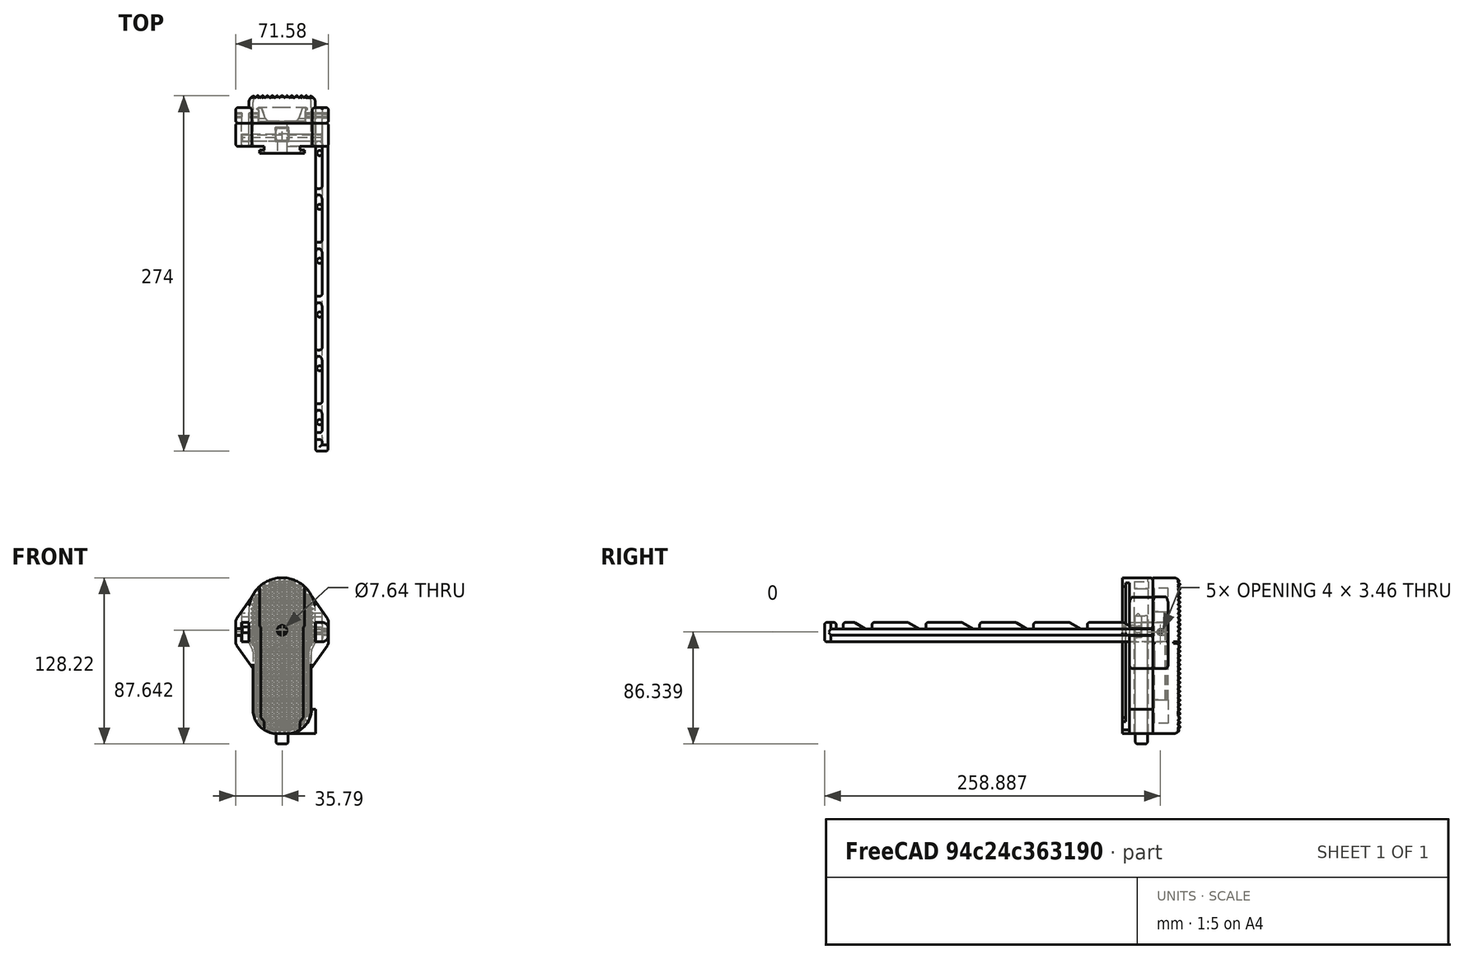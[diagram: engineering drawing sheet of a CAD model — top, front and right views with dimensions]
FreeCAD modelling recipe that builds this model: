
FCSTD DOCUMENT  (FreeCAD 0.19R24291 (Git))
Label: TelescopingButtExtensionPlasticArmsV2
License: All rights reserved
LicenseURL: http://en.wikipedia.org/wiki/All_rights_reserved
objects: Sketcher::SketchObject×34, PartDesign::Pocket×17, PartDesign::Pad×14, PartDesign::Fillet×10, PartDesign::Body×8, Spreadsheet::Sheet×5, PartDesign::Mirrored×4, PartDesign::LinearPattern×3, App::Part×3, Part::Mirroring×2, PartDesign::SubtractivePipe×1, PartDesign::AdditivePipe×1, PartDesign::Groove×1, PartDesign::Chamfer×1
note: 141 computed .brp shape members not serialized (recipe doc carries the construction recipe); baked Part::Feature solids carry a one-line shape summary decoded from their .brp

FEATURE [Spreadsheet::Sheet] Spreadsheet  label="P90Measurements"
  cells = A1=ButtDovetail; D1=Overall; G1=ButtPad; I1=Reference Point; J1=Bottom of pad, just at base of dovetail body; L1=SpaceForTelescopingBar; M1(SpaceForTelescopingBar)==0.584"; A2=DovetailHeight; B2(DovetailHeight)==5mm; D2=ButtOverallHeight; E2(ButtOverallHeight)==4.733"; G2=PadWidestWidth; H2(PadWidestWidth)==2.017"; A3=DovetailBodyWidth; B3(DovetailBodyWidth)==28mm; D3=PadBCGHoleFromReferencePoint; E3(PadBCGHoleFromReferencePoint)==2.997"; G3=PadThinnestWidth; H3(PadThinnestWidth)==1.772"; A4=DovetailLedgeHeight; B4(DovetailLedgeHeight)==2.5mm; D4=PadBCGHoleDiameter; E4(PadBCGHoleDiameter)==0.277"; G4=PadWidestWidthInnerShoulderDistanceFromReferencePoint; H4(PadWidestWidthInnerShoulderDistanceFromReferencePoint)==2.532"; A5=DovetailLedgeWidestWidth; B5(DovetailLedgeWidestWidth)==35.5mm; D5=PadBCGHoleDepth; E5(PadBCGHoleDepth)==0.375"; G5=PadWidestWidthOuterShoulderDistanceFromReferencePoint; H5(PadWidestWidthOuterShoulderDistanceFromReferencePoint)==2.785"; A6=DovetailLedgeMiddleWidth; B6(DovetailLedgeMiddleWidth)==1.32"; G6=PadBottomWidth; H6(PadBottomWidth)==0.3"; A7=DovetailMiddleWidthInsideShoulderDistanceFromReferencePoint; B7(DovetailMiddleWidthInsideShoulderDistanceFromReferencePoint)==0.37"; A8=DovetailMiddleWidthOutsideShoulderDistanceFromReferencePoint; B8(DovetailMiddleWidthOutsideShoulderDistanceFromReferencePoint)==0.484"; A9=DovetailBottobBodyBevelDistanceFromReferencePoint; B9(DovetailBottobBodyBevelDistanceFromReferencePoint)==0.154"; A10=DovetailWidestLedgeStartingPointFromReferencePoint; B10(DovetailWidestLedgeStartingPointFromReferencePoint)==3.222"
FEATURE [Spreadsheet::Sheet] Spreadsheet001  label="ProjectSettings"
  cells = A1=Tolerance; A2=LooseTolerance; B2(LooseTolerance)==0.3mm; C2=SpringMaxHeight; D2(SpringMaxHeight)==20mm; E2=CrosspinWidth; F2(CrosspinWidth)==4mm; G2=EndcapScrewBodyDiameter; H2(EndcapScrewBodyDiameter)==4mm; I2=LengthFromButtToChargingHandleShelf; J2(LengthFromButtToChargingHandleShelf)==310mm; K2=AdditionalPrinterTolerance; L2(AdditionalPrinterTolerance)==0mm; A3=TightTolerance; B3(TightTolerance)==0.1mm + AdditionalPrinterTolerance; C3=TelescopingPadOAL; D3(TelescopingPadOAL)==TelescopingBarInsertDepth + TelescopingButtThickness; E3=CrosspinHeight; F3(CrosspinHeight)==BarHeight / 3; G3=EndcapScrewHeadDiameter; H3(EndcapScrewHeadDiameter)==6mm; K3=SupportGap; L3(SupportGap)==0.16mm; A4=WallThickness; B4(WallThickness)==4mm; C4=StandardFillet; D4(StandardFillet)==2mm; E4=CrosspinLength; G4=EndcapNutHeight; H4(EndcapNutHeight)==0.273"; A5=LockingButtonWidth; B5(LockingButtonWidth)==10mm; C5=LockingPinWidth; D5(LockingPinWidth)==0.1875"; E5=ButtonActuationDistance; F5(ButtonActuationDistance)==CrosspinHeight * 2; G5=EndcapNutThickness; H5(EndcapNutThickness)==0.121"; A6=LockingButtonHeight; B6(LockingButtonHeight)==10mm; C6=LockingPinHeight; D6(LockingPinHeight)==BarHeight / 3 - LooseTolerance * 2; G6=EndcapSectionOnBarLength; H6(EndcapSectionOnBarLength)==15mm; A7=LockingButtonLength; B7(LockingButtonLength)==60mm; C7=LockingPinLength; D7(LockingPinLength)==40mm; G7=EndcapSectionHangingOffOfBarLength; H7(EndcapSectionHangingOffOfBarLength)==WallThickness; A8=LockingButtonHoleDepth; B8(LockingButtonHoleDepth)==<<P90Measurements>>.PadWidestWidthOuterShoulderDistanceFromReferencePoint + BarThickness + LockingPinHeight * 3 + SpringMaxHeight; C8=BarThickness; D8(BarThickness)==5mm; G8=ScrewCountersinkDepth; H8(ScrewCountersinkDepth)==0.089"; A9=LockingButtonActuationDistance; B9(LockingButtonActuationDistance)==6mm; C9=BarHeight; D9(BarHeight)==15mm; G9=EndcapScrewThreadHeight; H9(EndcapScrewThreadHeight)==8mm; A10=LockingBodyLength; B10(LockingBodyLength)==WallThickness * 2 + LockingButtonHeight; C10=BarLength; D10(BarLength)==265mm; A11=TelescopingPadComfortFilletRadius; B11(TelescopingPadComfortFilletRadius)==5mm; C11=BarNumberOfKnotches; D11(BarNumberOfKnotches)=6; C12=TelescopingBarInsertDepth; D12(TelescopingBarInsertDepth)==WallThickness * 2 + CrosspinWidth; A13=ScallopRadius; B13(ScallopRadius)==1.5mm; C13=TelescopingButtThickness; D13(TelescopingButtThickness)==10mm; A14=DistanceBetweenScallops; B14(DistanceBetweenScallops)==0.25mm; C14=BarDistanceBetweenKnotches; D14(BarDistanceBetweenKnotches)=; C15=BarLastKnotchLocationFromOrigin; D15(BarLastKnotchLocationFromOrigin)==BarLength - EndcapSectionOnBarLength - WallThickness; A16=PaperworkLidNubWidth; B16(PaperworkLidNubWidth)==2mm; C16=BarOccupiedLength; D16(BarOccupiedLength)==WallThickness * 4 + LockingButtonHeight + CrosspinWidth; A17=PaperworkLidNubHeight; B17(PaperworkLidNubHeight)==1.5mm; C17=BarUnoccupiedLength; D17(BarUnoccupiedLength)==BarLength - BarOccupiedLength; A18=PaperworkLidWallThickness; B18(PaperworkLidWallThickness)==2mm; C18=BarRackAngle; D18(BarRackAngle)=150; A19=PaperworkLidFingerHoleDiameter; B19(PaperworkLidFingerHoleDiameter)==20mm; C19=BarRackFillet; D19(BarRackFillet)==2mm; A20=PaperworkLipTabWallFilletRadius; B20(PaperworkLipTabWallFilletRadius)==4mm; C20=BarFillet; D20(BarFillet)==2mm; A21=PaperwokLipInteriorWallAngle; B21(PaperwokLipInteriorWallAngle)=110; C21=BarRackStartOffset; D21(BarRackStartOffset)==TelescopingBarInsertDepth + WallThickness + LockingButtonWidth / 2; A22=PaperworklidbaseThickness; B22(PaperworklidbaseThickness)==1.5mm; C22=BarRackEndoffset; D22(BarRackEndoffset)==WallThickness * 2 + LockingPinWidth + BarThickness; C23=BarRackL:ength; D23(BarRackLength)==13.6mm; A24=LockingButtonHoleClearanceForChamfer; B24(LockingButtonHoleClearanceForChamfer)==min(LockingButtonWidth; LockingButtonHeight) * 9 / 20; C24=BarEndcapThickness; D24(BarEndcapThickness)==BarThickness; A25=LockingPinPocketOverhangCompensationDistance; B25(LockingPinPocketOverhangCompensationDistance)==1.5mm; C25=PadCrosspinLength; D25(PadCrosspinLength)==17mm; A27=LockingBodyPadThickness; B27(LockingBodyPadThickness)==WallThickness * 2 + LockingButtonHeight
FEATURE [Sketcher::SketchObject] Sketch  label="DovetailBodySketch"
  FullyConstrained = true
  MapMode = 5
  Placement = pos=(0,0,0) rot=(1,0,0;1.5708rad)
  Support = -> [XZ_Plane]
  expr: Constraints[10] = <<P90Measurements>>.DovetailBodyWidth - <<ProjectSettings>>.LooseTolerance * 2
  expr: Constraints[9] = <<P90Measurements>>.ButtOverallHeight
  sketch-geometry (4):
    g0: LineSegment StartX=-13.7 StartY=120.218 StartZ=0 EndX=13.7 EndY=120.218 EndZ=0
    g1: LineSegment StartX=13.7 StartY=120.218 StartZ=0 EndX=13.7 EndY=0 EndZ=0
    g2: LineSegment StartX=13.7 StartY=0 StartZ=0 EndX=-13.7 EndY=0 EndZ=0
    g3: LineSegment StartX=-13.7 StartY=0 StartZ=0 EndX=-13.7 EndY=120.218 EndZ=0
  constraints (11):
    c: Coincident(g0,g1)
    c: Coincident(g1,g2)
    c: Coincident(g2,g3)
    c: Coincident(g3,g0)
    c: Horizontal(g0)
    c: Vertical(g1)
    c: Vertical(g3)
    c: PointOnObject(g1,g-1)
    c: Symmetric(g1,g2,g-2)
    c: DistanceY(g1,g1) = 120.218
    c: DistanceX(g0,g0) = 27.4
FEATURE [PartDesign::Pad] Pad  label="DovetailBodyPad"
  Direction = (1,1,1)
  Length = 5.2
  Length2 = 100
  Placement = pos=(0,0,0) rot=(1,0,0;1.5708rad)
  Profile = -> Sketch
  Type = 0
  expr: Length = <<P90Measurements>>.DovetailHeight + <<ProjectSettings>>.TightTolerance * 2
FEATURE [Sketcher::SketchObject] Sketch001  label="DovetailLedgeSketch"
  AttachmentOffset = pos=(0,0,5.2) rot=(0,0,1;0rad)
  FullyConstrained = true
  MapMode = 5
  Placement = pos=(0,-5.2,-1.2e-15) rot=(1,0,0;1.5708rad)
  Support = -> [XZ_Plane]
  expr: .AttachmentOffset.Base.z = <<DovetailBodyPad>>.Length
  expr: Constraints[10] = <<P90Measurements>>.DovetailLedgeWidestWidth - <<ProjectSettings>>.LooseTolerance * 2
  expr: Constraints[9] = <<P90Measurements>>.ButtOverallHeight
  sketch-geometry (4):
    g0: LineSegment StartX=-17.45 StartY=120.218 StartZ=0 EndX=17.45 EndY=120.218 EndZ=0
    g1: LineSegment StartX=17.45 StartY=120.218 StartZ=0 EndX=17.45 EndY=0 EndZ=0
    g2: LineSegment StartX=17.45 StartY=0 StartZ=0 EndX=-17.45 EndY=0 EndZ=0
    g3: LineSegment StartX=-17.45 StartY=0 StartZ=0 EndX=-17.45 EndY=120.218 EndZ=0
  constraints (11):
    c: Coincident(g0,g1)
    c: Coincident(g1,g2)
    c: Coincident(g2,g3)
    c: Coincident(g3,g0)
    c: Horizontal(g0)
    c: Vertical(g1)
    c: Vertical(g3)
    c: PointOnObject(g1,g-1)
    c: Symmetric(g2,g1,g-2)
    c: DistanceY(g1,g1) = 120.218
    c: DistanceX(g0,g0) = 34.9
FEATURE [PartDesign::Pad] Pad001  label="DovetailLedgePad"
  BaseFeature = -> Pad
  Direction = (1,1,1)
  Length = 2.3
  Length2 = 100
  Placement = pos=(0,0,0) rot=(1,0,0;1.5708rad)
  Profile = -> Sketch001
  Refine = true
  Reversed = true
  Type = 0
  expr: Length = <<P90Measurements>>.DovetailLedgeHeight - <<ProjectSettings>>.TightTolerance * 2
FEATURE [Sketcher::SketchObject] Sketch002  label="DovetailLedgeCutSketch"
  FullyConstrained = true
  MapMode = 5
  Placement = pos=(0,0,0) rot=(1,0,0;1.5708rad)
  Support = -> [XZ_Plane]
  expr: Constraints[35] = <<P90Measurements>>.DovetailMiddleWidthOutsideShoulderDistanceFromReferencePoint
  expr: Constraints[33] = <<P90Measurements>>.DovetailLedgeMiddleWidth - <<ProjectSettings>>.LooseTolerance * 2
  expr: Constraints[36] = <<P90Measurements>>.DovetailWidestLedgeStartingPointFromReferencePoint
  expr: Constraints[34] = <<P90Measurements>>.DovetailMiddleWidthInsideShoulderDistanceFromReferencePoint
  expr: Constraints[32] = <<P90Measurements>>.DovetailBodyWidth - <<ProjectSettings>>.LooseTolerance * 2
  expr: Constraints[29] = <<P90Measurements>>.DovetailLedgeWidestWidth - <<ProjectSettings>>.LooseTolerance * 2
  expr: Constraints[28] = <<P90Measurements>>.ButtOverallHeight
  sketch-geometry (16):
    g0: LineSegment StartX=-27.45 StartY=130.218 StartZ=0 EndX=27.45 EndY=130.218 EndZ=0
    g1: LineSegment StartX=27.45 StartY=130.218 StartZ=0 EndX=27.45 EndY=-10 EndZ=0
    g2: LineSegment StartX=27.45 StartY=-10 StartZ=0 EndX=-27.45 EndY=-10 EndZ=0
    g3: LineSegment StartX=-27.45 StartY=-10 StartZ=0 EndX=-27.45 EndY=130.218 EndZ=0
    g4: LineSegment StartX=-13.7 StartY=0 StartZ=0 EndX=13.7 EndY=0 EndZ=0
    g5: LineSegment StartX=13.7 StartY=0 StartZ=0 EndX=13.7 EndY=9.398 EndZ=0
    g6: LineSegment StartX=13.7 StartY=9.398 StartZ=0 EndX=16.464 EndY=12.2936 EndZ=0
    g7: LineSegment StartX=16.464 StartY=12.2936 StartZ=0 EndX=16.464 EndY=81.8388 EndZ=0
    g8: LineSegment StartX=16.464 StartY=81.8388 StartZ=0 EndX=17.45 EndY=82.8598 EndZ=0
    g9: LineSegment StartX=17.45 StartY=82.8598 StartZ=0 EndX=17.45 EndY=120.218 EndZ=0
    g10: LineSegment StartX=17.45 StartY=120.218 StartZ=0 EndX=-17.45 EndY=120.218 EndZ=0
    g11: LineSegment StartX=-17.45 StartY=120.218 StartZ=0 EndX=-17.45 EndY=82.8598 EndZ=0
    g12: LineSegment StartX=-17.45 StartY=82.8598 StartZ=0 EndX=-16.464 EndY=81.8388 EndZ=0
    g13: LineSegment StartX=-16.464 StartY=81.8388 StartZ=0 EndX=-16.464 EndY=12.2936 EndZ=0
    g14: LineSegment StartX=-16.464 StartY=12.2936 StartZ=0 EndX=-13.7 EndY=9.398 EndZ=0
    g15: LineSegment StartX=-13.7 StartY=9.398 StartZ=0 EndX=-13.7 EndY=0 EndZ=0
  constraints (44):
    c: Coincident(g0,g1)
    c: Coincident(g1,g2)
    c: Coincident(g2,g3)
    c: Coincident(g3,g0)
    c: Horizontal(g0)
    c: Horizontal(g2)
    c: Vertical(g1)
    c: Vertical(g3)
    c: PointOnObject(g4,g-1)
    c: Coincident(g4,g5)
    c: Vertical(g5)
    c: Coincident(g5,g6)
    c: Coincident(g6,g7)
    c: Vertical(g7)
    c: Coincident(g7,g8)
    c: Coincident(g8,g9)
    c: Vertical(g9)
    c: Coincident(g9,g10)
    c: Coincident(g10,g11)
    c: Coincident(g11,g12)
    c: Coincident(g12,g13)
    c: Vertical(g13)
    c: Coincident(g13,g14)
    c: Coincident(g14,g15)
    c: Coincident(g15,g4)
    c: Vertical(g15)
    c: Horizontal(g14,g5)
    c: Horizontal(g13,g6)
    c: DistanceY(g4,g9) = 120.218
    c: DistanceX(g10,g10) = 34.9
    c: Symmetric(g10,g9,g-2)
    c: Symmetric(g12,g7,g-2)
    c: DistanceX(g4,g4) = 27.4
    c: DistanceX(g12,g7) = 32.928
    c: DistanceY(g14) = 9.398
    c: DistanceY(g4,g13) = 12.2936
    c: DistanceY(g-1,g7) = 81.8388
    c: DistanceY(g10,g0) = 10
    c: DistanceX(g0,g10) = 10
    c: DistanceX(g9,g1) = 10
    c: DistanceY(g1,g4) = 10
    c: Symmetric(g4,g4,g-2)
    c: Symmetric(g8,g11,g-2)
    c: Angle(g12,g13) = 2.37365
FEATURE [PartDesign::Pocket] Pocket  label="DovetailLedgeCutPocket"
  BaseFeature = -> Pad001
  Length = 5
  Length2 = 100
  Placement = pos=(0,0,0) rot=(1,0,0;1.5708rad)
  Profile = -> Sketch002
  Reversed = true
  Type = 1
FEATURE [Sketcher::SketchObject] Sketch003  label="PadBodySketch"
  FullyConstrained = true
  MapMode = 5
  Placement = pos=(0,0,0) rot=(1,0,0;1.5708rad)
  Support = -> [XZ_Plane]
  expr: Constraints[27] = <<P90Measurements>>.PadWidestWidthInnerShoulderDistanceFromReferencePoint
  expr: Constraints[22] = <<P90Measurements>>.PadWidestWidthOuterShoulderDistanceFromReferencePoint
  expr: Constraints[19] = <<P90Measurements>>.PadThinnestWidth
  expr: Constraints[21] = <<P90Measurements>>.PadWidestWidth
  expr: Constraints[20] = <<P90Measurements>>.ButtOverallHeight
  sketch-geometry (12):
    g0: LineSegment StartX=-22.5044 StartY=0 StartZ=0 EndX=22.5044 EndY=0 EndZ=0
    g1: LineSegment StartX=22.5044 StartY=0 StartZ=0 EndX=22.5044 EndY=63.2152 EndZ=0
    g2: LineSegment StartX=-22.5044 StartY=63.2152 StartZ=0 EndX=-22.5044 EndY=0 EndZ=0
    g3: LineSegment StartX=-25.6159 StartY=120.218 StartZ=0 EndX=25.6159 EndY=120.218 EndZ=0
    g4: LineSegment StartX=25.6159 StartY=120.218 StartZ=0 EndX=25.6159 EndY=70.739 EndZ=0
    g5: LineSegment StartX=-25.6159 StartY=70.739 StartZ=0 EndX=-25.6159 EndY=120.218 EndZ=0
    g6: LineSegment StartX=-25.3621 StartY=69.6414 StartZ=0 EndX=-22.7582 EndY=64.3128 EndZ=0
    g7: LineSegment StartX=25.3621 StartY=69.6414 StartZ=0 EndX=22.7582 EndY=64.3128 EndZ=0
    g8: ArcOfCircle CenterX=-23.1159 CenterY=70.739 CenterZ=0 NormalX=0 NormalY=0 NormalZ=1 AngleXU=0 Radius=2.5 StartAngle=3.14159 EndAngle=3.59612
    g9: ArcOfCircle CenterX=-25.0044 CenterY=63.2152 CenterZ=0 NormalX=0 NormalY=0 NormalZ=1 AngleXU=0 Radius=2.5 StartAngle=2e-16 EndAngle=0.454529
    g10: ArcOfCircle CenterX=23.1159 CenterY=70.739 CenterZ=0 NormalX=0 NormalY=0 NormalZ=1 AngleXU=0 Radius=2.5 StartAngle=5.82866 EndAngle=6.28319
    g11: ArcOfCircle CenterX=25.0044 CenterY=63.2152 CenterZ=0 NormalX=0 NormalY=0 NormalZ=1 AngleXU=0 Radius=2.5 StartAngle=2.68706 EndAngle=3.14159
  constraints (28):
    c: Coincident(g0,g1)
    c: Coincident(g2,g0)
    c: Vertical(g1)
    c: Vertical(g2)
    c: PointOnObject(g0,g-1)
    c: Coincident(g3,g4)
    c: Coincident(g5,g3)
    c: Vertical(g4)
    c: Vertical(g5)
    c: Tangent(g8,g5) = 1.5708
    c: Tangent(g8,g6) = -1.5708
    c: Tangent(g9,g6) = 1.5708
    c: Tangent(g11,g1) = 1.5708
    c: Tangent(g11,g7) = -1.5708
    c: Tangent(g7,g10) = 1.5708
    c: Tangent(g10,g4) = 1.5708
    c: Tangent(g9,g2) = 1.5708
    c: Symmetric(g0,g0,g-2)
    c: Symmetric(g3,g3,g-2)
    c: DistanceX(g0,g0) = 45.0088
    c: DistanceY(g0,g3) = 120.218
    c: DistanceX(g3,g3) = 51.2318
    c: DistanceY(g-1,g8) = 70.739
    c: Symmetric(g7,g6,g-2)
    c: Symmetric(g6,g7,g-2)
    c: Equal(g11,g10)
    c: Diameter(g11) = 5
    c: DistanceY(g6) = 64.3128
FEATURE [PartDesign::Pad] Pad002  label="PadBodyPad"
  BaseFeature = -> Pocket
  Direction = (1,1,1)
  Length = 18
  Length2 = 100
  Placement = pos=(0,0,0) rot=(1,0,0;1.5708rad)
  Profile = -> Sketch003
  Reversed = true
  Type = 0
  expr: Length = <<ProjectSettings>>.LockingBodyPadThickness
FEATURE [Sketcher::SketchObject] Sketch004  label="PadBevelsCutSketch"
  FullyConstrained = true
  MapMode = 5
  Placement = pos=(0,0,0) rot=(1,0,0;1.5708rad)
  Support = -> [XZ_Plane]
  expr: Constraints[32] = <<P90Measurements>>.PadBottomWidth
  expr: Constraints[29] = <<P90Measurements>>.PadWidestWidth
  expr: Constraints[31] = <<P90Measurements>>.PadWidestWidthInnerShoulderDistanceFromReferencePoint - 5mm
  expr: Constraints[30] = <<P90Measurements>>.PadThinnestWidth
  expr: Constraints[27] = <<P90Measurements>>.ButtOverallHeight
  sketch-geometry (15):
    g0: LineSegment StartX=-35.6159 StartY=130.218 StartZ=0 EndX=35.6159 EndY=130.218 EndZ=0
    g1: LineSegment StartX=35.6159 StartY=130.218 StartZ=0 EndX=35.6159 EndY=-10 EndZ=0
    g2: LineSegment StartX=35.6159 StartY=-10 StartZ=0 EndX=-35.6159 EndY=-10 EndZ=0
    g3: LineSegment StartX=-35.6159 StartY=-10 StartZ=0 EndX=-35.6159 EndY=130.218 EndZ=0
    g4: ArcOfCircle CenterX=-3.81 CenterY=18.6944 CenterZ=0 NormalX=0 NormalY=0 NormalZ=1 AngleXU=0 Radius=18.6944 StartAngle=3.14159 EndAngle=4.71239
    g5: ArcOfCircle CenterX=3.81 CenterY=18.6944 CenterZ=0 NormalX=0 NormalY=0 NormalZ=1 AngleXU=0 Radius=18.6944 StartAngle=4.71239 EndAngle=6.28319
    g6: ArcOfCircle CenterX=2.5e-15 CenterY=94.6023 CenterZ=0 NormalX=0 NormalY=0 NormalZ=1 AngleXU=0 Radius=25.6159 StartAngle=1.5708 EndAngle=3.14159
    g7: ArcOfCircle CenterX=2.5e-15 CenterY=94.6023 CenterZ=0 NormalX=0 NormalY=0 NormalZ=1 AngleXU=0 Radius=25.6159 StartAngle=0 EndAngle=1.5708
    g8: LineSegment StartX=-25.6159 StartY=94.6023 StartZ=0 EndX=-25.6159 EndY=59.3128 EndZ=0
    g9: LineSegment StartX=-25.6159 StartY=59.3128 StartZ=0 EndX=-22.5044 EndY=59.3128 EndZ=0
    g10: LineSegment StartX=-22.5044 StartY=59.3128 StartZ=0 EndX=-22.5044 EndY=18.6944 EndZ=0
    g11: LineSegment StartX=-3.81 StartY=0 StartZ=0 EndX=3.81 EndY=0 EndZ=0
    g12: LineSegment StartX=22.5044 StartY=18.6944 StartZ=0 EndX=22.5044 EndY=59.3128 EndZ=0
    g13: LineSegment StartX=22.5044 StartY=59.3128 StartZ=0 EndX=25.6159 EndY=59.3128 EndZ=0
    g14: LineSegment StartX=25.6159 StartY=59.3128 StartZ=0 EndX=25.6159 EndY=94.6023 EndZ=0
  constraints (39):
    c: Coincident(g0,g1)
    c: Coincident(g1,g2)
    c: Coincident(g2,g3)
    c: Coincident(g3,g0)
    c: Horizontal(g0)
    c: Vertical(g1)
    c: Vertical(g3)
    c: Symmetric(g2,g1,g-2)
    c: PointOnObject(g4,g-1)
    c: PointOnObject(g5,g-1)
    c: Vertical(g8)
    c: Coincident(g9,g8)
    c: Vertical(g10)
    c: Vertical(g12)
    c: Coincident(g13,g12)
    c: Vertical(g14)
    c: Coincident(g13,g14)
    c: Horizontal(g13)
    c: Tangent(g6,g8) = -1.5708
    c: Tangent(g7,g14) = -1.5708
    c: Tangent(g10,g4) = -1.5708
    c: Tangent(g11,g4) = -1.5708
    c: Tangent(g11,g5) = -1.5708
    c: Tangent(g12,g5) = -1.5708
    c: Symmetric(g12,g10,g-2)
    c: Symmetric(g8,g13,g-2)
    c: Coincident(g10,g9)
    c: DistanceY(g-1,g7) = 120.218
    c: Equal(g5,g4)
    c: DistanceX(g6,g7) = 51.2318
    c: DistanceX(g9,g12) = 45.0088
    c: DistanceY(g-1,g12) = 59.3128
    c: DistanceX(g11,g11) = 7.62
    c: PointOnObject(g6,g-2)
    c: Tangent(g6,g7) = -1.5708
    c: Equal(g8,g14)
    c: DistanceY(g2,g-1) = 10
    c: DistanceY(g6,g0) = 10
    c: DistanceX(g7,g1) = 10
FEATURE [PartDesign::Pocket] Pocket001  label="PadBevelsCutPocket"
  BaseFeature = -> Pad002
  Length = 5
  Length2 = 100
  Midplane = true
  Placement = pos=(0,0,0) rot=(1,0,0;1.5708rad)
  Profile = -> Sketch004
  Type = 1
FEATURE [Spreadsheet::Sheet] Spreadsheet002  label="TelescopingBarSettings"
  cells = A1=BarOffsetFromCenter; B1(BarOffsetFromCenter)==<<PadBodyPad>>.Length + <<TelescoptingPadBodyPad>>.Length; A2=LengthFromButtToChargingHandleShelf; B2(LengthFromButtToChargingHandleShelf)==310mm; A3=BarLength; B3(BarLength)==270mm; A4=BarThickness; B4(BarThickness)==0.125"; A5=CrosspinThickness; B5(CrosspinThickness)==0.125"; A6=BarHeight; B6(BarHeight)==12.7mm; A7=LockingPinThickness; B7(LockingPinThickness)==0.125"; A8=BarNumberOfKnotches; B8(BarNumberOfKnotches)=6; A9=ScrewCountersinkDepth; B9(ScrewCountersinkDepth)==0.089"; A10=EndcapHexnutHeight; B10(EndcapHexnutHeight)==0.273"; A11=EndcapHexnutThickness; B11(EndcapHexnutThickness)==0.121"; A12=CrosspinHeight; B12(CrosspinHeight)==6mm; A13=LockingPinHeight; B13(LockingPinHeight)==6mm
FEATURE [Sketcher::SketchObject] Sketch008  label="TelescoptingPadBodySketch"
  FullyConstrained = true
  MapMode = 5
  Placement = pos=(0,0,0) rot=(1,0,0;1.5708rad)
  Support = -> [XZ_Plane002]
  expr: Constraints[20] = <<P90Measurements>>.ButtOverallHeight
  expr: Constraints[21] = <<P90Measurements>>.PadWidestWidth
  expr: Constraints[19] = <<P90Measurements>>.PadThinnestWidth
  expr: Constraints[22] = <<P90Measurements>>.PadWidestWidthOuterShoulderDistanceFromReferencePoint
  expr: Constraints[27] = <<P90Measurements>>.PadWidestWidthInnerShoulderDistanceFromReferencePoint
  sketch-geometry (12):
    g0: LineSegment StartX=-22.5044 StartY=0 StartZ=0 EndX=22.5044 EndY=0 EndZ=0
    g1: LineSegment StartX=22.5044 StartY=0 StartZ=0 EndX=22.5044 EndY=63.2152 EndZ=0
    g2: LineSegment StartX=-22.5044 StartY=63.2152 StartZ=0 EndX=-22.5044 EndY=0 EndZ=0
    g3: LineSegment StartX=-25.6159 StartY=120.218 StartZ=0 EndX=25.6159 EndY=120.218 EndZ=0
    g4: LineSegment StartX=25.6159 StartY=120.218 StartZ=0 EndX=25.6159 EndY=70.739 EndZ=0
    g5: LineSegment StartX=-25.6159 StartY=70.739 StartZ=0 EndX=-25.6159 EndY=120.218 EndZ=0
    g6: LineSegment StartX=-25.3621 StartY=69.6414 StartZ=0 EndX=-22.7582 EndY=64.3128 EndZ=0
    g7: LineSegment StartX=25.3621 StartY=69.6414 StartZ=0 EndX=22.7582 EndY=64.3128 EndZ=0
    g8: ArcOfCircle CenterX=-23.1159 CenterY=70.739 CenterZ=0 NormalX=0 NormalY=0 NormalZ=1 AngleXU=0 Radius=2.5 StartAngle=3.14159 EndAngle=3.59612
    g9: ArcOfCircle CenterX=-25.0044 CenterY=63.2152 CenterZ=0 NormalX=0 NormalY=0 NormalZ=1 AngleXU=0 Radius=2.5 StartAngle=0 EndAngle=0.454529
    g10: ArcOfCircle CenterX=23.1159 CenterY=70.739 CenterZ=0 NormalX=0 NormalY=0 NormalZ=1 AngleXU=0 Radius=2.5 StartAngle=5.82866 EndAngle=6.28319
    g11: ArcOfCircle CenterX=25.0044 CenterY=63.2152 CenterZ=0 NormalX=0 NormalY=0 NormalZ=1 AngleXU=0 Radius=2.5 StartAngle=2.68706 EndAngle=3.14159
  constraints (29):
    c: Coincident(g0,g1)
    c: Coincident(g2,g0)
    c: Vertical(g1)
    c: Vertical(g2)
    c: PointOnObject(g0,g-1)
    c: Coincident(g3,g4)
    c: Coincident(g5,g3)
    c: Vertical(g4)
    c: Vertical(g5)
    c: Tangent(g8,g5) = 1.5708
    c: Tangent(g8,g6) = -1.5708
    c: Tangent(g9,g6) = 1.5708
    c: Tangent(g11,g1) = 1.5708
    c: Tangent(g11,g7) = -1.5708
    c: Tangent(g7,g10) = 1.5708
    c: Tangent(g10,g4) = 1.5708
    c: Tangent(g9,g2) = 1.5708
    c: Symmetric(g0,g0,g-2)
    c: Symmetric(g3,g3,g-2)
    c: DistanceX(g0,g0) = 45.0088
    c: DistanceY(g0,g3) = 120.218
    c: DistanceX(g3,g3) = 51.2318
    c: DistanceY(g-1,g8) = 70.739
    c: Symmetric(g7,g6,g-2)
    c: Symmetric(g6,g7,g-2)
    c: Equal(g11,g10)
    c: Diameter(g11) = 5
    c: DistanceY(g6) = 64.3128
    c: Angle(g1,g7) = 2.68706  'PadAngle'
FEATURE [PartDesign::Pad] Pad006  label="TelescoptingPadBodyPad"
  Direction = (1,1,1)
  Length = 21
  Length2 = 100
  Placement = pos=(0,0,0) rot=(1,0,0;1.5708rad)
  Profile = -> Sketch008
  Reversed = true
  Type = 0
  expr: Length = <<ProjectSettings>>.TelescopingBarInsertDepth + <<ProjectSettings>>.WallThickness + <<ProjectSettings>>.TelescopingPadComfortFilletRadius
FEATURE [Sketcher::SketchObject] Sketch009  label="TelescopingPadBevelsCutSketch"
  FullyConstrained = true
  MapMode = 5
  Placement = pos=(0,0,0) rot=(1,0,0;1.5708rad)
  Support = -> [XZ_Plane002]
  expr: Constraints[27] = <<P90Measurements>>.ButtOverallHeight
  expr: Constraints[30] = <<P90Measurements>>.PadThinnestWidth
  expr: Constraints[31] = <<P90Measurements>>.PadWidestWidthInnerShoulderDistanceFromReferencePoint - 5mm
  expr: Constraints[29] = <<P90Measurements>>.PadWidestWidth
  expr: Constraints[32] = <<P90Measurements>>.PadBottomWidth
  sketch-geometry (15):
    g0: LineSegment StartX=-35.6159 StartY=130.218 StartZ=0 EndX=35.6159 EndY=130.218 EndZ=0
    g1: LineSegment StartX=35.6159 StartY=130.218 StartZ=0 EndX=35.6159 EndY=-10 EndZ=0
    g2: LineSegment StartX=35.6159 StartY=-10 StartZ=0 EndX=-35.6159 EndY=-10 EndZ=0
    g3: LineSegment StartX=-35.6159 StartY=-10 StartZ=0 EndX=-35.6159 EndY=130.218 EndZ=0
    g4: ArcOfCircle CenterX=-3.81 CenterY=18.6944 CenterZ=0 NormalX=0 NormalY=0 NormalZ=1 AngleXU=0 Radius=18.6944 StartAngle=3.14159 EndAngle=4.71239
    g5: ArcOfCircle CenterX=3.81 CenterY=18.6944 CenterZ=0 NormalX=0 NormalY=0 NormalZ=1 AngleXU=0 Radius=18.6944 StartAngle=4.71239 EndAngle=6.28319
    g6: ArcOfCircle CenterX=8e-16 CenterY=94.6023 CenterZ=0 NormalX=0 NormalY=0 NormalZ=1 AngleXU=0 Radius=25.6159 StartAngle=1.5708 EndAngle=3.14159
    g7: ArcOfCircle CenterX=8e-16 CenterY=94.6023 CenterZ=0 NormalX=0 NormalY=0 NormalZ=1 AngleXU=0 Radius=25.6159 StartAngle=0 EndAngle=1.5708
    g8: LineSegment StartX=-25.6159 StartY=94.6023 StartZ=0 EndX=-25.6159 EndY=59.3128 EndZ=0
    g9: LineSegment StartX=-25.6159 StartY=59.3128 StartZ=0 EndX=-22.5044 EndY=59.3128 EndZ=0
    g10: LineSegment StartX=-22.5044 StartY=59.3128 StartZ=0 EndX=-22.5044 EndY=18.6944 EndZ=0
    g11: LineSegment StartX=-3.81 StartY=0 StartZ=0 EndX=3.81 EndY=0 EndZ=0
    g12: LineSegment StartX=22.5044 StartY=18.6944 StartZ=0 EndX=22.5044 EndY=59.3128 EndZ=0
    g13: LineSegment StartX=22.5044 StartY=59.3128 StartZ=0 EndX=25.6159 EndY=59.3128 EndZ=0
    g14: LineSegment StartX=25.6159 StartY=59.3128 StartZ=0 EndX=25.6159 EndY=94.6023 EndZ=0
  constraints (39):
    c: Coincident(g0,g1)
    c: Coincident(g1,g2)
    c: Coincident(g2,g3)
    c: Coincident(g3,g0)
    c: Horizontal(g0)
    c: Vertical(g1)
    c: Vertical(g3)
    c: Symmetric(g2,g1,g-2)
    c: PointOnObject(g4,g-1)
    c: PointOnObject(g5,g-1)
    c: Vertical(g8)
    c: Coincident(g9,g8)
    c: Vertical(g10)
    c: Vertical(g12)
    c: Coincident(g13,g12)
    c: Vertical(g14)
    c: Coincident(g13,g14)
    c: Horizontal(g13)
    c: Tangent(g6,g8) = -1.5708
    c: Tangent(g7,g14) = -1.5708
    c: Tangent(g10,g4) = -1.5708
    c: Tangent(g11,g4) = -1.5708
    c: Tangent(g11,g5) = -1.5708
    c: Tangent(g12,g5) = -1.5708
    c: Symmetric(g12,g10,g-2)
    c: Symmetric(g8,g13,g-2)
    c: Coincident(g10,g9)
    c: DistanceY(g-1,g7) = 120.218
    c: Equal(g5,g4)
    c: DistanceX(g6,g7) = 51.2318
    c: DistanceX(g9,g12) = 45.0088
    c: DistanceY(g-1,g12) = 59.3128
    c: DistanceX(g11,g11) = 7.62
    c: PointOnObject(g6,g-2)
    c: Tangent(g6,g7) = -1.5708
    c: Equal(g8,g14)
    c: DistanceY(g2,g-1) = 10
    c: DistanceY(g6,g0) = 10
    c: DistanceX(g7,g1) = 10
FEATURE [PartDesign::Pocket] Pocket002  label="TelescopingPadBevelsCutPocket"
  BaseFeature = -> Pad006
  Length = 5
  Length2 = 100
  Midplane = true
  Placement = pos=(0,0,0) rot=(1,0,0;1.5708rad)
  Profile = -> Sketch009
  Type = 1
FEATURE [Sketcher::SketchObject] Sketch010  label="TelescopingBarInsertArmSketch"
  FullyConstrained = true
  MapMode = 5
  Placement = pos=(0,0,0) rot=(1,0,0;1.5708rad)
  Support = -> [XZ_Plane002]
  expr: Constraints[11] = <<ProjectSettings>>.BarHeight + <<ProjectSettings>>.TightTolerance * 2
  expr: Constraints[13] = <<P90Measurements>>.PadThinnestWidth / 2
  expr: Constraints[8] = <<P90Measurements>>.PadWidestWidth / 2
  expr: Constraints[10] = <<P90Measurements>>.PadWidestWidthOuterShoulderDistanceFromReferencePoint
  expr: Constraints[9] = <<ProjectSettings>>.BarThickness + <<ProjectSettings>>.LooseTolerance * 2
  expr: Constraints[27] = <<ProjectSettings>>.BarThickness + <<ProjectSettings>>.TightTolerance * 2
  sketch-geometry (13):
    g0: LineSegment StartX=31.2159 StartY=70.739 StartZ=0 EndX=31.2159 EndY=85.939 EndZ=0
    g1: LineSegment StartX=30.8159 StartY=85.939 StartZ=0 EndX=25.6159 EndY=85.939 EndZ=0
    g2: LineSegment StartX=25.6159 StartY=85.939 StartZ=0 EndX=25.6159 EndY=70.739 EndZ=0
    g3: LineSegment StartX=25.6159 StartY=70.739 StartZ=0 EndX=30.8159 EndY=70.739 EndZ=0
    g4: LineSegment StartX=35.7859 StartY=70.739 StartZ=0 EndX=35.7859 EndY=86.039 EndZ=0
    g5: LineSegment StartX=22.5044 StartY=106.448 StartZ=0 EndX=22.5044 EndY=50.3301 EndZ=0
    g6: ArcOfCircle CenterX=31.2159 CenterY=70.739 CenterZ=0 NormalX=0 NormalY=0 NormalZ=1 AngleXU=0 Radius=4.57 StartAngle=5.67232 EndAngle=6.28319
    g7: LineSegment StartX=22.5044 StartY=50.3301 StartZ=0 EndX=34.9594 EndY=68.1178 EndZ=0
    g8: LineSegment StartX=22.5044 StartY=106.448 StartZ=0 EndX=34.9594 EndY=88.6602 EndZ=0
    g9: ArcOfCircle CenterX=31.2159 CenterY=86.039 CenterZ=0 NormalX=0 NormalY=0 NormalZ=1 AngleXU=0 Radius=4.57 StartAngle=4e-16 EndAngle=0.610865
    g10: LineSegment StartX=30.8159 StartY=85.939 StartZ=0 EndX=30.8159 EndY=70.739 EndZ=0
    g11: LineSegment StartX=30.8159 StartY=70.739 StartZ=0 EndX=31.2159 EndY=70.739 EndZ=0
    g12: LineSegment StartX=30.8159 StartY=85.939 StartZ=0 EndX=31.2159 EndY=85.939 EndZ=0
  constraints (36):
    c: Vertical(g0)
    c: Horizontal(g1)
    c: Coincident(g1,g2)
    c: Vertical(g2)
    c: Coincident(g2,g3)
    c: Vertical(g5)
    c: Vertical(g4)
    c: Horizontal(g3)
    c: DistanceX(g-1,g2) = 25.6159
    c: DistanceX(g1,g0) = 5.6
    c: DistanceY(g-1,g2) = 70.739
    c: DistanceY(g0,g0) = 15.2
    c: Coincident(g6,g0)
    c: DistanceX(g-1,g5) = 22.5044
    c: Coincident(g7,g5)
    c: Coincident(g8,g5)
    c: Tangent(g6,g4) = -1.5708
    c: Tangent(g7,g6) = -1.5708
    c: Equal(g7,g8)
    c: Angle(g4,g7) = 2.53073
    c: DistanceX(g-1,g4) = 35.7859  'DistanceFromCenterlineToOutsideOfBarInsertArm'
    c: PointOnObject(g9,g0)
    c: DistanceY(g0,g9) = 0.1
    c: Tangent(g9,g8) = 1.5708
    c: Tangent(g9,g4) = -1.5708
    c: Diameter(g9) = 9.14
    c: Vertical(g10)
    c: DistanceX(g1,g10) = 5.2
    c: Coincident(g1,g10)
    c: Coincident(g3,g10)
    c: Coincident(g11,g3)
    c: Coincident(g11,g6)
    c: Coincident(g12,g1)
    c: Coincident(g12,g0)
    c: Horizontal(g12)
    c: Horizontal(g11)
FEATURE [Spreadsheet::Sheet] Spreadsheet003  label="TelescopingPadSettings"
  cells = A1=TelescopingBarInsertDepth; B1(TelescopingBarInsertDepth)==<<ProjectSettings>>.WallThickness * 2 + <<TelescopingBarSettings>>.CrosspinThickness + <<ProjectSettings>>.TightTolerance * 2; A2=TelescopingButtThickness; B2(TelescopingButtThickness)==10mm; A3=TelescopingPadOAL; B3(TelescopingPadOAL)==TelescopingBarInsertDepth + TelescopingButtThickness
FEATURE [PartDesign::Pad] Pad007  label="TelescopingBarInsertArmPad"
  BaseFeature = -> Pocket002
  Direction = (1,1,1)
  Length = 12
  Length2 = 100
  Placement = pos=(0,0,0) rot=(1,0,0;1.5708rad)
  Profile = -> Sketch010
  Reversed = true
  Type = 0
  expr: Length = <<ProjectSettings>>.TelescopingBarInsertDepth
FEATURE [Sketcher::SketchObject] Sketch011  label="CrosspinHoleSketch"
  FullyConstrained = true
  MapMode = 5
  Placement = pos=(0,0,0) rot=(0.57735,0.57735,0.57735;2.0944rad)
  Support = -> [YZ_Plane002]
  expr: Constraints[2] = <<ProjectSettings>>.CrosspinWidth
  expr: Constraints[0] = <<P90Measurements>>.PadWidestWidthOuterShoulderDistanceFromReferencePoint + <<ProjectSettings>>.BarHeight / 2 + <<ProjectSettings>>.TightTolerance
  expr: Constraints[1] = <<TelescopingPadSettings>>.TelescopingBarInsertDepth / 2 + <<ProjectSettings>>.TightTolerance * 2
  sketch-geometry (8):
    g0: Circle CenterX=5.8875 CenterY=78.339 CenterZ=0 NormalX=0 NormalY=0 NormalZ=1 AngleXU=0 Radius=2
    g1: LineSegment StartX=4.8875 StartY=80.0711 StartZ=0 EndX=3.8875 EndY=78.339 EndZ=0
    g2: LineSegment StartX=3.8875 StartY=78.339 StartZ=0 EndX=4.8875 EndY=76.6069 EndZ=0
    g3: LineSegment StartX=4.8875 StartY=76.6069 StartZ=0 EndX=6.8875 EndY=76.6069 EndZ=0
    g4: LineSegment StartX=6.8875 StartY=76.6069 StartZ=0 EndX=7.8875 EndY=78.339 EndZ=0
    g5: LineSegment StartX=7.8875 StartY=78.339 StartZ=0 EndX=6.8875 EndY=80.0711 EndZ=0
    g6: LineSegment StartX=6.8875 StartY=80.0711 StartZ=0 EndX=4.8875 EndY=80.0711 EndZ=0
    g7: Circle CenterX=5.8875 CenterY=78.339 CenterZ=0 NormalX=0 NormalY=0 NormalZ=1 AngleXU=0 Radius=2
  constraints (19):
    c: DistanceY(g-1,g0) = 78.339
    c: DistanceX(g-1,g0) = 5.8875
    c: Diameter(g0) = 4
    c: Coincident(g1,g2)
    c: Coincident(g2,g3)
    c: Coincident(g3,g4)
    c: Coincident(g4,g5)
    c: Coincident(g5,g6)
    c: Coincident(g6,g1)
    c: Equal(g1, g2-g6) x5
    c: PointOnObject(g1,g7)
    c: PointOnObject(g2,g7)
    c: PointOnObject(g3,g7)
    c: PointOnObject(g4,g7)
    c: PointOnObject(g5,g7)
    c: PointOnObject(g6,g7)
    c: Coincident(g7,g0)
    c: Horizontal(g1,g4)
    c: Equal(g7,g0)
FEATURE [PartDesign::Mirrored] Mirrored  label="TelescopingBarInsertArmMirror"
  BaseFeature = -> Pad007
  MirrorPlane = -> Sketch010 [V_Axis]
  Originals = -> [Pad007]
  Placement = pos=(0,0,0) rot=(1,0,0;1.5708rad)
FEATURE [PartDesign::Pocket] Pocket003  label="CrosspinHolePocket"
  BaseFeature = -> Mirrored
  Length = 5
  Length2 = 100
  Midplane = true
  Placement = pos=(0,0,0) rot=(1,0,0;1.5708rad)
  Profile = -> Sketch011
  Type = 1
FEATURE [PartDesign::Fillet] Fillet  label="ComfortFillet"
  Base = -> Pocket003 [Edge86]
  BaseFeature = -> Pocket003
  Placement = pos=(0,0,0) rot=(1,0,0;1.5708rad)
  Radius = 5
  SupportTransform = false
  expr: Radius = <<ProjectSettings>>.TelescopingPadComfortFilletRadius
FEATURE [Spreadsheet::Sheet] Spreadsheet004  label="CentralPadSettings"
  cells = A1=PadThickness; B1(PadThickness)==<<PadBodyPad>>.Length; A2=LockingButtonHoleDepth; B2(LockingButtonHoleDepth)==<<P90Measurements>>.PadWidestWidthOuterShoulderDistanceFromReferencePoint + <<TelescopingBarSettings>>.BarThickness + <<TelescopingBarSettings>>.LockingPinHeight * 3 + SpringMaxHeight; A3=SpringMaxHeight; B3(SpringMaxHeight)==20mm
FEATURE [Sketcher::SketchObject] Sketch014  label="CentralPadTelescopingBarInsertArmSketch"
  FullyConstrained = true
  MapMode = 5
  Placement = pos=(0,0,0) rot=(1,0,0;1.5708rad)
  Support = -> [XZ_Plane]
  expr: Constraints[11] = <<ProjectSettings>>.BarThickness + <<ProjectSettings>>.LooseTolerance * 2
  expr: Constraints[12] = <<P90Measurements>>.PadWidestWidthOuterShoulderDistanceFromReferencePoint
  expr: Constraints[10] = <<P90Measurements>>.PadWidestWidth / 2
  expr: Constraints[13] = <<ProjectSettings>>.BarHeight + <<ProjectSettings>>.TightTolerance * 2
  expr: Constraints[16] = <<P90Measurements>>.PadThinnestWidth / 2
  expr: Constraints[34] = <<ProjectSettings>>.BarHeight / 3 + <<ProjectSettings>>.TightTolerance * 2
  sketch-geometry (14):
    g0: LineSegment StartX=31.2159 StartY=70.739 StartZ=0 EndX=31.2159 EndY=75.739 EndZ=0
    g1: LineSegment StartX=31.2159 StartY=85.939 StartZ=0 EndX=25.6159 EndY=85.939 EndZ=0
    g2: LineSegment StartX=25.6159 StartY=85.939 StartZ=0 EndX=25.6159 EndY=70.739 EndZ=0
    g3: LineSegment StartX=25.6159 StartY=70.739 StartZ=0 EndX=31.2159 EndY=70.739 EndZ=0
    g4: LineSegment StartX=35.7859 StartY=70.739 StartZ=0 EndX=35.7859 EndY=75.739 EndZ=0
    g5: LineSegment StartX=22.5044 StartY=106.348 StartZ=0 EndX=22.5044 EndY=50.3301 EndZ=0
    g6: ArcOfCircle CenterX=31.2159 CenterY=85.939 CenterZ=0 NormalX=0 NormalY=0 NormalZ=1 AngleXU=0 Radius=4.57 StartAngle=2.3e-15 EndAngle=0.610865
    g7: ArcOfCircle CenterX=31.2159 CenterY=70.739 CenterZ=0 NormalX=0 NormalY=0 NormalZ=1 AngleXU=0 Radius=4.57 StartAngle=5.67232 EndAngle=6.28319
    g8: LineSegment StartX=22.5044 StartY=50.3301 StartZ=0 EndX=34.9594 EndY=68.1178 EndZ=0
    g9: LineSegment StartX=22.5044 StartY=106.348 StartZ=0 EndX=34.9594 EndY=88.5602 EndZ=0
    g10: LineSegment StartX=31.2159 StartY=80.939 StartZ=0 EndX=35.7859 EndY=80.939 EndZ=0
    g11: LineSegment StartX=31.2159 StartY=75.739 StartZ=0 EndX=35.7859 EndY=75.739 EndZ=0
    g12: LineSegment StartX=31.2159 StartY=80.939 StartZ=0 EndX=31.2159 EndY=85.939 EndZ=0
    g13: LineSegment StartX=35.7859 StartY=80.939 StartZ=0 EndX=35.7859 EndY=85.939 EndZ=0
  constraints (38):
    c: Vertical(g0)
    c: Coincident(g12,g1)
    c: Horizontal(g1)
    c: Coincident(g1,g2)
    c: Vertical(g2)
    c: Coincident(g2,g3)
    c: Coincident(g3,g0)
    c: Vertical(g5)
    c: Vertical(g4)
    c: Horizontal(g3)
    c: DistanceX(g-1,g2) = 25.6159
    c: DistanceX(g1,g1) = 5.6
    c: DistanceY(g-1,g2) = 70.739
    c: DistanceY(g0,g12) = 15.2
    c: Coincident(g6,g12)
    c: Coincident(g7,g0)
    c: DistanceX(g-1,g5) = 22.5044
    c: Coincident(g8,g5)
    c: Coincident(g9,g5)
    c: Tangent(g7,g4) = -1.5708
    c: Tangent(g9,g6) = 1.5708
    c: Tangent(g8,g7) = -1.5708
    c: Diameter(g6) = 9.14
    c: Equal(g8,g9)
    c: Angle(g4,g8) = 2.53073
    c: Horizontal(g11)
    c: Horizontal(g10)
    c: Coincident(g0,g11)
    c: Coincident(g12,g10)
    c: Tangent(g0,g12)
    c: Coincident(g4,g11)
    c: Coincident(g13,g10)
    c: Tangent(g4,g13)
    c: Tangent(g6,g13) = -1.5708
    c: DistanceY(g4,g10) = 5.2
    c: Equal(g12,g0)
    c: Angle(g5,g9) = 0.610865  'BarArmAngle'
    c: DistanceX(g10,g10) = 4.57  'BarArmWallThickness'
FEATURE [PartDesign::Pad] Pad008  label="CentralPadTelescopingBarInsertArmPad"
  BaseFeature = -> Pocket001
  Direction = (1,1,1)
  Length = 18
  Length2 = 100
  Placement = pos=(0,0,0) rot=(1,0,0;1.5708rad)
  Profile = -> Sketch014
  Reversed = true
  Type = 0
  expr: Length = <<CentralPadSettings>>.PadThickness
FEATURE [PartDesign::Mirrored] Mirrored001  label="CentralPadTelescopingBarInsertArmMirror"
  BaseFeature = -> Pad008
  MirrorPlane = -> Sketch014 [V_Axis]
  Originals = -> [Pad008]
  Placement = pos=(0,0,0) rot=(1,0,0;1.5708rad)
FEATURE [Sketcher::SketchObject] Sketch017  label="LockingPinBodySketch"
  FullyConstrained = true
  MapMode = 5
  Placement = pos=(0,0,0) rot=(0.57735,0.57735,0.57735;2.0944rad)
  Support = -> [YZ_Plane005]
  expr: Constraints[9] = <<ProjectSettings>>.LockingPinHeight
  expr: Constraints[6] = <<ProjectSettings>>.LockingPinWidth
  sketch-geometry (4):
    g0: LineSegment StartX=-2.38125 StartY=2.2 StartZ=0 EndX=2.38125 EndY=2.2 EndZ=0
    g1: LineSegment StartX=2.38125 StartY=2.2 StartZ=0 EndX=2.38125 EndY=-2.2 EndZ=0
    g2: LineSegment StartX=2.38125 StartY=-2.2 StartZ=0 EndX=-2.38125 EndY=-2.2 EndZ=0
    g3: LineSegment StartX=-2.38125 StartY=-2.2 StartZ=0 EndX=-2.38125 EndY=2.2 EndZ=0
  constraints (10):
    c: Coincident(g0,g1)
    c: Coincident(g1,g2)
    c: Coincident(g2,g3)
    c: Coincident(g3,g0)
    c: Horizontal(g2)
    c: Vertical(g1)
    c: DistanceX(g0,g0) = 4.7625
    c: Symmetric(g2,g0,g-1)
    c: Symmetric(g0,g0,g-2)
    c: DistanceY(g3,g3) = 4.4
FEATURE [PartDesign::Pad] Pad010  label="LockingPinBodyPad"
  Direction = (1,1,1)
  Length = 61.4468
  Length2 = 100
  Midplane = true
  Placement = pos=(0,0,0) rot=(0.57735,0.57735,0.57735;2.0944rad)
  Profile = -> Sketch017
  Type = 0
  expr: Length = Sketch010.Constraints.DistanceFromCenterlineToOutsideOfBarInsertArm * 2 - <<TelescopingBarSettings>>.BarThickness * 3 - <<ProjectSettings>>.LooseTolerance * 2
FEATURE [Sketcher::SketchObject] Sketch018  label="LockingPinHoleSketch"
  FullyConstrained = true
  MapMode = 5
  Placement = pos=(0,0,0) rot=(0.57735,0.57735,0.57735;2.0944rad)
  Support = -> [YZ_Plane]
  expr: Constraints[8] = <<ProjectSettings>>.LockingPinWidth + <<ProjectSettings>>.LooseTolerance * 2
  expr: Constraints[9] = <<P90Measurements>>.PadWidestWidthOuterShoulderDistanceFromReferencePoint + (<<TelescopingBarSettings>>.BarHeight - <<TelescopingBarSettings>>.LockingPinHeight) / 2
  expr: Constraints[10] = <<ProjectSettings>>.WallThickness
  expr: Constraints[11] = <<P90Measurements>>.PadWidestWidthOuterShoulderDistanceFromReferencePoint + <<TelescopingBarSettings>>.BarHeight + <<TelescopingBarSettings>>.LockingPinHeight + <<ProjectSettings>>.LooseTolerance * 2
  sketch-geometry (4):
    g0: LineSegment StartX=4 StartY=90.039 StartZ=0 EndX=9.3625 EndY=90.039 EndZ=0
    g1: LineSegment StartX=9.3625 StartY=90.039 StartZ=0 EndX=9.3625 EndY=74.089 EndZ=0
    g2: LineSegment StartX=9.3625 StartY=74.089 StartZ=0 EndX=4 EndY=74.089 EndZ=0
    g3: LineSegment StartX=4 StartY=74.089 StartZ=0 EndX=4 EndY=90.039 EndZ=0
  constraints (12):
    c: Coincident(g0,g1)
    c: Coincident(g1,g2)
    c: Coincident(g2,g3)
    c: Coincident(g3,g0)
    c: Horizontal(g0)
    c: Horizontal(g2)
    c: Vertical(g1)
    c: Vertical(g3)
    c: DistanceX(g0,g0) = 5.3625
    c: DistanceY(g-1,g2) = 74.089
    c: DistanceX(g-1,g2) = 4
    c: DistanceY(g-1,g0) = 90.039
FEATURE [PartDesign::Pocket] Pocket007  label="LockingPinHolePocket"
  BaseFeature = -> Mirrored001
  Length = 62.0468
  Length2 = 100
  Midplane = true
  Placement = pos=(0,0,0) rot=(1,0,0;1.5708rad)
  Profile = -> Sketch018
  Type = 0
  expr: Length = <<LockingPinBodyPad>>.Length + <<ProjectSettings>>.LooseTolerance * 2
FEATURE [Sketcher::SketchObject] Sketch019  label="LockingButtonHoleSketch"
  FullyConstrained = true
  MapMode = 5
  Support = -> [XY_Plane]
  expr: Constraints[18] = <<ProjectSettings>>.WallThickness
  expr: Constraints[16] = <<ProjectSettings>>.LockingButtonHeight + <<ProjectSettings>>.LooseTolerance * 2
  expr: Constraints[17] = <<ProjectSettings>>.LockingButtonWidth + <<ProjectSettings>>.LooseTolerance * 2
  expr: Constraints[14] = <<ProjectSettings>>.StandardFillet
  sketch-geometry (8):
    g0: LineSegment StartX=-3.3 StartY=14.6 StartZ=0 EndX=3.3 EndY=14.6 EndZ=0
    g1: LineSegment StartX=5.3 StartY=12.6 StartZ=0 EndX=5.3 EndY=6 EndZ=0
    g2: LineSegment StartX=3.3 StartY=4 StartZ=0 EndX=-3.3 EndY=4 EndZ=0
    g3: LineSegment StartX=-5.3 StartY=6 StartZ=0 EndX=-5.3 EndY=12.6 EndZ=0
    g4: ArcOfCircle CenterX=-3.3 CenterY=12.6 CenterZ=0 NormalX=0 NormalY=0 NormalZ=1 AngleXU=0 Radius=2 StartAngle=1.5708 EndAngle=3.14159
    g5: ArcOfCircle CenterX=3.3 CenterY=12.6 CenterZ=0 NormalX=0 NormalY=0 NormalZ=1 AngleXU=0 Radius=2 StartAngle=0 EndAngle=1.5708
    g6: ArcOfCircle CenterX=3.3 CenterY=6 CenterZ=0 NormalX=0 NormalY=0 NormalZ=1 AngleXU=0 Radius=2 StartAngle=4.71239 EndAngle=6.28319
    g7: ArcOfCircle CenterX=-3.3 CenterY=6 CenterZ=0 NormalX=0 NormalY=0 NormalZ=1 AngleXU=0 Radius=2 StartAngle=3.14159 EndAngle=4.71239
  constraints (19):
    c: Horizontal(g2)
    c: Vertical(g1)
    c: Vertical(g3)
    c: Tangent(g3,g4) = 1.5708
    c: Tangent(g0,g4) = 1.5708
    c: Tangent(g0,g5) = 1.5708
    c: Tangent(g1,g5) = 1.5708
    c: Tangent(g2,g6) = 1.5708
    c: Tangent(g1,g6) = 1.5708
    c: Tangent(g2,g7) = 1.5708
    c: Tangent(g3,g7) = 1.5708
    c: Equal(g7,g4)
    c: Equal(g4,g5)
    c: Equal(g5,g6)
    c: Radius(g5) = 2
    c: Symmetric(g0,g0,g-2)
    c: DistanceY(g2,g0) = 10.6
    c: DistanceX(g3,g1) = 10.6
    c: DistanceY(g-1,g2) = 4
FEATURE [PartDesign::Pocket] Pocket008  label="LockingButtonHolePocket"
  BaseFeature = -> Pocket007
  Length = 111.914
  Length2 = 100
  Placement = pos=(0,0,0) rot=(1,0,0;1.5708rad)
  Profile = -> Sketch019
  Reversed = true
  Type = 0
  expr: Length = <<CentralPadSettings>>.LockingButtonHoleDepth
FEATURE [Sketcher::SketchObject] Sketch020  label="ButtonBodySketch"
  AttachmentOffset = pos=(0,0,2) rot=(0,0,1;0rad)
  FullyConstrained = true
  MapMode = 5
  Placement = pos=(0,0,2) rot=(0,0,1;0rad)
  Support = -> [XY_Plane006]
  expr: Constraints[10] = <<ProjectSettings>>.StandardFillet
  expr: Constraints[16] = <<ProjectSettings>>.LockingButtonWidth - <<ProjectSettings>>.LooseTolerance * 2
  expr: Constraints[17] = <<ProjectSettings>>.LockingButtonWidth - <<ProjectSettings>>.LooseTolerance * 2
  sketch-geometry (8):
    g0: LineSegment StartX=-2.7 StartY=4.7 StartZ=0 EndX=2.7 EndY=4.7 EndZ=0
    g1: LineSegment StartX=4.7 StartY=2.7 StartZ=0 EndX=4.7 EndY=-2.7 EndZ=0
    g2: LineSegment StartX=2.7 StartY=-4.7 StartZ=0 EndX=-2.7 EndY=-4.7 EndZ=0
    g3: LineSegment StartX=-4.7 StartY=-2.7 StartZ=0 EndX=-4.7 EndY=2.7 EndZ=0
    g4: ArcOfCircle CenterX=-2.7 CenterY=2.7 CenterZ=0 NormalX=0 NormalY=0 NormalZ=1 AngleXU=0 Radius=2 StartAngle=1.5708 EndAngle=3.14159
    g5: ArcOfCircle CenterX=2.7 CenterY=2.7 CenterZ=0 NormalX=0 NormalY=0 NormalZ=1 AngleXU=0 Radius=2 StartAngle=0 EndAngle=1.5708
    g6: ArcOfCircle CenterX=2.7 CenterY=-2.7 CenterZ=0 NormalX=0 NormalY=0 NormalZ=1 AngleXU=0 Radius=2 StartAngle=4.71239 EndAngle=6.28319
    g7: ArcOfCircle CenterX=-2.7 CenterY=-2.7 CenterZ=0 NormalX=0 NormalY=0 NormalZ=1 AngleXU=0 Radius=2 StartAngle=3.14159 EndAngle=4.71239
  constraints (18):
    c: Horizontal(g0)
    c: Vertical(g1)
    c: Tangent(g3,g4) = 1.5708
    c: Tangent(g0,g4) = 1.5708
    c: Tangent(g1,g5) = 1.5708
    c: Tangent(g0,g5) = 1.5708
    c: Tangent(g1,g6) = 1.5708
    c: Tangent(g2,g6) = 1.5708
    c: Tangent(g2,g7) = 1.5708
    c: Tangent(g3,g7) = 1.5708
    c: Radius(g4) = 2
    c: Equal(g4,g5)
    c: Equal(g4,g6)
    c: Equal(g4,g7)
    c: Symmetric(g2,g2,g-2)
    c: Symmetric(g3,g3,g-1)
    c: DistanceX(g3,g1) = 9.4
    c: DistanceY(g2,g0) = 9.4
FEATURE [PartDesign::Pad] Pad011  label="ButtonBodyPad"
  Direction = (1,1,1)
  Length = 88.939
  Length2 = 10
  Profile = -> Sketch020
  Type = 4
  expr: Length2 = <<ProjectSettings>>.LockingButtonActuationDistance + 4mm
  expr: Length = <<ProjectSettings>>.LockingButtonHoleDepth - <<ProjectSettings>>.SpringMaxHeight
FEATURE [Sketcher::SketchObject] Sketch021  label="ButtonLockingPinHoleSketch"
  FullyConstrained = true
  MapMode = 5
  Placement = pos=(0,0,0) rot=(0.57735,0.57735,0.57735;2.0944rad)
  Support = -> [YZ_Plane006]
  expr: Constraints[11] = <<ProjectSettings>>.LockingPinHeight + <<ProjectSettings>>.TightTolerance * 2
  expr: Constraints[9] = (<<ProjectSettings>>.LockingButtonWidth - <<ProjectSettings>>.LooseTolerance * 2) / 2
  expr: Constraints[7] = <<ProjectSettings>>.LockingPinWidth + <<ProjectSettings>>.TightTolerance * 2
  expr: Constraints[8] = <<P90Measurements>>.PadWidestWidthOuterShoulderDistanceFromReferencePoint + <<ProjectSettings>>.BarHeight / 2
  sketch-geometry (4):
    g0: LineSegment StartX=-4.7 StartY=82.839 StartZ=0 EndX=0.2625 EndY=82.839 EndZ=0
    g1: LineSegment StartX=0.2625 StartY=82.839 StartZ=0 EndX=0.2625 EndY=78.239 EndZ=0
    g2: LineSegment StartX=0.2625 StartY=78.239 StartZ=0 EndX=-4.7 EndY=78.239 EndZ=0
    g3: LineSegment StartX=-4.7 StartY=78.239 StartZ=0 EndX=-4.7 EndY=82.839 EndZ=0
  constraints (12):
    c: Coincident(g0,g1)
    c: Coincident(g1,g2)
    c: Coincident(g2,g3)
    c: Coincident(g3,g0)
    c: Horizontal(g2)
    c: Vertical(g1)
    c: Vertical(g3)
    c: DistanceX(g0,g0) = 4.9625
    c: DistanceY(g-1,g2) = 78.239
    c: DistanceX(g2,g-1) = 4.7
    c: Horizontal(g0)
    c: DistanceY(g3,g3) = 4.6
FEATURE [PartDesign::Pocket] Pocket009  label="ButtonLockingPinHolePocket"
  BaseFeature = -> Pad011
  Length = 5
  Length2 = 100
  Midplane = true
  Profile = -> Sketch021
  Type = 1
FEATURE [Sketcher::SketchObject] Sketch022  label="BCGHoleSketch"
  AttachmentOffset = pos=(0,0,5.2) rot=(0,0,1;0rad)
  FullyConstrained = true
  MapMode = 5
  Placement = pos=(0,-5.2,-1.2e-15) rot=(1,0,0;1.5708rad)
  Support = -> [XZ_Plane]
  expr: Constraints[1] = <<P90Measurements>>.PadBCGHoleFromReferencePoint + <<P90Measurements>>.PadBCGHoleDiameter / 2
  expr: Constraints[2] = <<P90Measurements>>.PadBCGHoleDiameter + <<ProjectSettings>>.LooseTolerance * 2
  expr: .AttachmentOffset.Base.z = <<DovetailBodyPad>>.Length
  sketch-geometry (1):
    g0: Circle CenterX=0 CenterY=79.6417 CenterZ=0 NormalX=0 NormalY=0 NormalZ=1 AngleXU=0 Radius=3.8179
  constraints (3):
    c: PointOnObject(g0,g-2)
    c: DistanceY(g-1,g0) = 79.6417
    c: Diameter(g0) = 7.6358
FEATURE [PartDesign::Pocket] Pocket010  label="BCGHolePocket"
  BaseFeature = -> Pocket008
  Length = 9.2
  Length2 = 100
  Placement = pos=(0,0,0) rot=(1,0,0;1.5708rad)
  Profile = -> Sketch022
  Refine = true
  Type = 0
  expr: Length = <<DovetailBodyPad>>.Length + <<ProjectSettings>>.WallThickness
FEATURE [Sketcher::SketchObject] Sketch024  label="BarCrosspinHoleSketch001"
  FullyConstrained = true
  MapMode = 5
  Placement = pos=(0,0,0) rot=(0.57735,0.57735,0.57735;2.0944rad)
  Support = -> [YZ_Plane007]
  expr: Constraints[2] = <<ProjectSettings>>.WallThickness + <<ProjectSettings>>.CrosspinWidth / 2 + <<ProjectSettings>>.TightTolerance
  expr: Constraints[1] = <<ProjectSettings>>.CrosspinWidth
  sketch-geometry (8):
    g0: Circle CenterX=-6.1 CenterY=0 CenterZ=0 NormalX=0 NormalY=0 NormalZ=1 AngleXU=0 Radius=2
    g1: LineSegment StartX=-4.1 StartY=-2.6457e-12 StartZ=0 EndX=-5.1 EndY=1.73205 EndZ=0
    g2: LineSegment StartX=-5.1 StartY=1.73205 StartZ=0 EndX=-7.1 EndY=1.73205 EndZ=0
    g3: LineSegment StartX=-7.1 StartY=1.73205 StartZ=0 EndX=-8.1 EndY=-2.6457e-12 EndZ=0
    g4: LineSegment StartX=-8.1 StartY=-2.6457e-12 StartZ=0 EndX=-7.1 EndY=-1.73205 EndZ=0
    g5: LineSegment StartX=-7.1 StartY=-1.73205 StartZ=0 EndX=-5.1 EndY=-1.73205 EndZ=0
    g6: LineSegment StartX=-5.1 StartY=-1.73205 StartZ=0 EndX=-4.1 EndY=-2.6457e-12 EndZ=0
    g7: Circle CenterX=-6.1 CenterY=0 CenterZ=0 NormalX=0 NormalY=0 NormalZ=1 AngleXU=0 Radius=2
  constraints (19):
    c: PointOnObject(g0,g-1)
    c: Diameter(g0) = 4
    c: DistanceX(g0,g-1) = 6.1
    c: Coincident(g1,g2)
    c: Coincident(g2,g3)
    c: Coincident(g3,g4)
    c: Coincident(g4,g5)
    c: Coincident(g5,g6)
    c: Coincident(g6,g1)
    c: Equal(g1, g2-g6) x5
    c: PointOnObject(g1,g7)
    c: PointOnObject(g2,g7)
    c: PointOnObject(g3,g7)
    c: PointOnObject(g4,g7)
    c: PointOnObject(g5,g7)
    c: PointOnObject(g6,g7)
    c: Coincident(g7,g0)
    c: PointOnObject(g6,g0)
    c: Horizontal(g1,g3)
FEATURE [Sketcher::SketchObject] Sketch025  label="MainBarSketch001"
  FullyConstrained = true
  MapMode = 5
  Placement = pos=(0,0,0) rot=(1,0,0;1.5708rad)
  Support = -> [XZ_Plane007]
  expr: Constraints[9] = <<ProjectSettings>>.BarHeight
  expr: Constraints[8] = <<ProjectSettings>>.BarThickness
  sketch-geometry (4):
    g0: LineSegment StartX=-2.5 StartY=7.5 StartZ=0 EndX=2.5 EndY=7.5 EndZ=0
    g1: LineSegment StartX=2.5 StartY=7.5 StartZ=0 EndX=2.5 EndY=-7.5 EndZ=0
    g2: LineSegment StartX=2.5 StartY=-7.5 StartZ=0 EndX=-2.5 EndY=-7.5 EndZ=0
    g3: LineSegment StartX=-2.5 StartY=-7.5 StartZ=0 EndX=-2.5 EndY=7.5 EndZ=0
  constraints (10):
    c: Coincident(g0,g1)
    c: Coincident(g1,g2)
    c: Coincident(g2,g3)
    c: Coincident(g3,g0)
    c: Horizontal(g2)
    c: Vertical(g3)
    c: Symmetric(g1,g0,g-1)
    c: Symmetric(g0,g0,g-2)
    c: DistanceX(g0,g0) = 5
    c: DistanceY(g3,g3) = 15
FEATURE [PartDesign::Pad] Pad013  label="MainBarPad001"
  Direction = (1,1,1)
  Length = 265
  Length2 = 100
  Placement = pos=(0,0,0) rot=(1,0,0;1.5708rad)
  Profile = -> Sketch025
  Type = 0
  expr: Length = <<ProjectSettings>>.BarLength
FEATURE [PartDesign::Pocket] Pocket011  label="BarCrosspinHolePocket001"
  BaseFeature = -> Pad013
  Length = 5
  Length2 = 100
  Midplane = true
  Placement = pos=(0,0,0) rot=(1,0,0;1.5708rad)
  Profile = -> Sketch024
  Type = 1
FEATURE [Sketcher::SketchObject] Sketch027  label="BarRackSketch001"
  FullyConstrained = true
  MapMode = 5
  Placement = pos=(0,0,0) rot=(0.57735,0.57735,0.57735;2.0944rad)
  Support = -> [YZ_Plane007]
  expr: Constraints[18] = <<ProjectSettings>>.BarRackLength
  expr: Constraints[14] = <<ProjectSettings>>.BarRackStartOffset
  expr: Constraints[13] = <<ProjectSettings>>.BarRackFillet
  expr: Constraints[8] = <<ProjectSettings>>.BarRackFillet
  expr: Constraints[3] = <<ProjectSettings>>.BarHeight / 2
  expr: Constraints[4] = <<ProjectSettings>>.BarHeight / 3
  expr: Constraints[2] = <<ProjectSettings>>.LockingPinWidth + <<ProjectSettings>>.TightTolerance * 2
  sketch-geometry (7):
    g0: LineSegment StartX=-35.1371 StartY=-7.5 StartZ=0 EndX=-19 EndY=-7.5 EndZ=0
    g1: LineSegment StartX=-21 StartY=-2.5 StartZ=0 EndX=-25.9625 EndY=-2.5 EndZ=0
    g2: ArcOfCircle CenterX=-35.1371 CenterY=-5.5 CenterZ=0 NormalX=0 NormalY=0 NormalZ=1 AngleXU=0 Radius=2 StartAngle=4.71239 EndAngle=5.23713
    g3: LineSegment StartX=-34.1352 StartY=-7.23091 StartZ=0 EndX=-25.9625 EndY=-2.5 EndZ=0
    g4: LineSegment StartX=-21 StartY=-2.5 StartZ=0 EndX=-21 EndY=-5.5 EndZ=0
    g5: ArcOfCircle CenterX=-19 CenterY=-5.5 CenterZ=0 NormalX=0 NormalY=0 NormalZ=1 AngleXU=0 Radius=2 StartAngle=3.14159 EndAngle=4.71239
    g6: LineSegment StartX=-34.1352 StartY=-7.23091 StartZ=0 EndX=-34.6 EndY=-7.5 EndZ=0
  constraints (19):
    c: Horizontal(g0)
    c: Horizontal(g1)
    c: DistanceX(g1,g1) = 4.9625
    c: DistanceY(g0,g-1) = 7.5
    c: DistanceY(g0,g1) = 5
    c: Tangent(g0,g2) = -1.5708
    c: Coincident(g3,g1)
    c: Tangent(g3,g2) = -1.5708
    c: Radius(g2) = 2
    c: Coincident(g4,g1)
    c: Vertical(g4)
    c: Tangent(g5,g4) = -1.5708
    c: Tangent(g0,g5) = -1.5708
    c: Radius(g5) = 2
    c: DistanceX(g1,g-1) = 21
    c: Coincident(g6,g2)
    c: PointOnObject(g6,g0)
    c: Tangent(g6,g2)
    c: DistanceX(g6,g4) = 13.6
FEATURE [PartDesign::Pocket] Pocket013  label="BarRackPocket001"
  BaseFeature = -> Pocket011
  Length = 5
  Length2 = 100
  Midplane = true
  Placement = pos=(0,0,0) rot=(1,0,0;1.5708rad)
  Profile = -> Sketch027
  Type = 1
FEATURE [Sketcher::SketchObject] Sketch028  label="FinalSlotSketch001"
  FullyConstrained = true
  MapMode = 5
  Placement = pos=(0,0,0) rot=(0.57735,0.57735,0.57735;2.0944rad)
  Support = -> [YZ_Plane007]
  expr: Constraints[14] = <<ProjectSettings>>.BarRackFillet
  expr: Constraints[3] = -1 * <<ProjectSettings>>.BarHeight / 2
  expr: Constraints[4] = <<ProjectSettings>>.BarHeight / 3
  expr: Constraints[2] = <<ProjectSettings>>.LockingPinWidth + <<ProjectSettings>>.LooseTolerance * 2
  expr: Constraints[5] = <<ProjectSettings>>.BarLength - <<ProjectSettings>>.BarThickness - <<ProjectSettings>>.WallThickness
  sketch-geometry (6):
    g0: LineSegment StartX=-248.637 StartY=-7.5 StartZ=0 EndX=-258 EndY=-7.5 EndZ=0
    g1: LineSegment StartX=-256 StartY=-2.5 StartZ=0 EndX=-250.637 EndY=-2.5 EndZ=0
    g2: ArcOfCircle CenterX=-258 CenterY=-5.5 CenterZ=0 NormalX=0 NormalY=0 NormalZ=1 AngleXU=0 Radius=2 StartAngle=4.71239 EndAngle=6.28319
    g3: ArcOfCircle CenterX=-248.637 CenterY=-5.5 CenterZ=0 NormalX=0 NormalY=0 NormalZ=1 AngleXU=0 Radius=2 StartAngle=3.14159 EndAngle=4.71239
    g4: LineSegment StartX=-250.637 StartY=-2.5 StartZ=0 EndX=-250.637 EndY=-5.5 EndZ=0
    g5: LineSegment StartX=-256 StartY=-2.5 StartZ=0 EndX=-256 EndY=-5.5 EndZ=0
  constraints (16):
    c: Horizontal(g0)
    c: Horizontal(g1)
    c: DistanceX(g1,g1) = 5.3625
    c: DistanceY(g-1,g0) = -7.5
    c: DistanceY(g0,g1) = 5
    c: DistanceX(g1,g-1) = 256
    c: Coincident(g4,g1)
    c: Vertical(g4)
    c: Coincident(g5,g1)
    c: Vertical(g5)
    c: Tangent(g2,g5) = 1.5708
    c: Tangent(g3,g4) = -1.5708
    c: Tangent(g0,g3) = 1.5708
    c: Tangent(g0,g2) = 1.5708
    c: Radius(g3) = 2
    c: Equal(g3,g2)
FEATURE [PartDesign::LinearPattern] LinearPattern001  label="BarRackPattern001"
  BaseFeature = -> Pocket013
  Direction = -> Sketch027 [H_Axis]
  Length = 207.4
  Occurrences = 6
  Originals = -> [Pocket013]
  Placement = pos=(0,0,0) rot=(1,0,0;1.5708rad)
  Reversed = true
  expr: Occurrences = floor(Length / (<<ProjectSettings>>.BarRackLength + <<CentralPadTelescopingBarInsertArmPad>>.Length))
  expr: Length = <<ProjectSettings>>.BarLength - <<ProjectSettings>>.BarRackStartOffset - <<CentralPadTelescopingBarInsertArmPad>>.Length - <<ProjectSettings>>.BarEndcapThickness - <<ProjectSettings>>.BarRackLength
FEATURE [PartDesign::Pocket] Pocket012  label="FinalSlotPad001"
  BaseFeature = -> LinearPattern001
  Length = 5
  Length2 = 100
  Midplane = true
  Placement = pos=(0,0,0) rot=(1,0,0;1.5708rad)
  Profile = -> Sketch028
  Refine = true
  Type = 1
FEATURE [PartDesign::Fillet] Fillet004  label="Slide Fillet"
  Base = -> Pad010 [Edge8]
  BaseFeature = -> Pad010
  Placement = pos=(0,0,0) rot=(0.57735,0.57735,0.57735;2.0944rad)
  Radius = 2
  SupportTransform = false
FEATURE [Sketcher::SketchObject] Sketch029  label="LightningCutSketch"
  FullyConstrained = true
  MapMode = 5
  Placement = pos=(0,0,0) rot=(1,0,0;1.5708rad)
  Support = -> [XZ_Plane002]
  expr: Constraints[2] = <<P90Measurements>>.PadWidestWidth - <<ProjectSettings>>.TelescopingPadComfortFilletRadius * 3
  expr: Constraints[5] = <<P90Measurements>>.ButtOverallHeight - <<ProjectSettings>>.WallThickness * 2
  expr: Constraints[11] = <<ProjectSettings>>.WallThickness * 2
  sketch-geometry (6):
    g0: ArcOfCircle CenterX=-1.1391e-12 CenterY=26.1159 CenterZ=0 NormalX=0 NormalY=0 NormalZ=1 AngleXU=0 Radius=18.1159 StartAngle=3.14159 EndAngle=4.71239
    g1: LineSegment StartX=18.1159 StartY=26.1159 StartZ=0 EndX=18.1159 EndY=94.1023 EndZ=0
    g2: LineSegment StartX=-18.1159 StartY=26.1159 StartZ=0 EndX=-18.1159 EndY=94.1023 EndZ=0
    g3: ArcOfCircle CenterX=-6.2e-15 CenterY=94.1023 CenterZ=0 NormalX=0 NormalY=0 NormalZ=1 AngleXU=0 Radius=18.1159 StartAngle=1.5708 EndAngle=3.14159
    g4: ArcOfCircle CenterX=-6.2e-15 CenterY=94.1023 CenterZ=0 NormalX=0 NormalY=0 NormalZ=1 AngleXU=0 Radius=18.1159 StartAngle=0 EndAngle=1.5708
    g5: ArcOfCircle CenterX=2.401e-13 CenterY=26.1159 CenterZ=0 NormalX=0 NormalY=0 NormalZ=1 AngleXU=0 Radius=18.1159 StartAngle=4.71239 EndAngle=6.28319
  constraints (15):
    c: Vertical(g2)
    c: Vertical(g1)
    c: DistanceX(g2,g1) = 36.2318
    c: Tangent(g2,g3) = 1.5708
    c: Tangent(g1,g4) = -1.5708
    c: DistanceY(g-1,g3) = 112.218
    c: Tangent(g4,g3) = -1.5708
    c: PointOnObject(g3,g-2)
    c: Symmetric(g2,g1,g-2)
    c: Tangent(g1,g5) = -1.5708
    c: Tangent(g0,g2) = 1.5708
    c: DistanceY(g-1,g5) = 8
    c: Tangent(g0,g5) = -1.5708
    c: PointOnObject(g0,g-2)
    c: Horizontal(g0,g1)
FEATURE [PartDesign::Pocket] Pocket014  label="LightningCutPocket"
  BaseFeature = -> Fillet
  Length = 12
  Length2 = 100
  Placement = pos=(0,0,0) rot=(1,0,0;1.5708rad)
  Profile = -> Sketch029
  Type = 0
  expr: Length = <<ProjectSettings>>.TelescopingBarInsertDepth
FEATURE [PartDesign::Fillet] Fillet016  label="BarHoleLargeFillet"
  Base = -> Pocket010 [Edge203,Edge186,Edge187,Edge204,Edge49,Edge75,Edge48,Edge74,Edge217,Edge123]
  BaseFeature = -> Pocket010
  Placement = pos=(0,0,0) rot=(1,0,0;1.5708rad)
  Radius = 2
  SupportTransform = false
FEATURE [PartDesign::Fillet] Fillet017  label="LockingBodytHardEdgeFillet"
  Base = -> Fillet016 [Edge1,Edge68,Edge133,Edge164]
  BaseFeature = -> Fillet016
  Placement = pos=(0,0,0) rot=(1,0,0;1.5708rad)
  Radius = 2
  SupportTransform = false
FEATURE [PartDesign::Fillet] Fillet018
  Base = -> Pocket009 [Face2]
  BaseFeature = -> Pocket009
  Radius = 2
  SupportTransform = false
FEATURE [PartDesign::Body] Body005  label="LockingButton"
  Group = -> [Sketch020,Pad011,Sketch021,Pocket009,Fillet018]
  Origin = -> Origin006
  Placement = pos=(0,9.3,0) rot=(0,0,1;0rad)
  Tip = -> Fillet018
  expr: .Placement.Base.y = <<ProjectSettings>>.LockingButtonHeight / 2 + <<ProjectSettings>>.WallThickness + <<ProjectSettings>>.LooseTolerance
FEATURE [Sketcher::SketchObject] Sketch040  label="HorizontalScallopSketch"
  FullyConstrained = true
  MapMode = 5
  Placement = pos=(0,0,0) rot=(0.57735,0.57735,0.57735;2.0944rad)
  Support = -> [YZ_Plane002]
  expr: Constraints[1] = <<ProjectSettings>>.ScallopRadius
  expr: Constraints[2] = <<TelescoptingPadBodyPad>>.Length
  sketch-geometry (5):
    g0: Circle CenterX=21 CenterY=0 CenterZ=0 NormalX=0 NormalY=0 NormalZ=1 AngleXU=0 Radius=1.5
    g1: LineSegment StartX=21 StartY=1.5 StartZ=0 EndX=19.5 EndY=0 EndZ=0
    g2: LineSegment StartX=19.5 StartY=0 StartZ=0 EndX=21 EndY=-1.5 EndZ=0
    g3: LineSegment StartX=21 StartY=-1.5 StartZ=0 EndX=22.5 EndY=0 EndZ=0
    g4: LineSegment StartX=22.5 StartY=0 StartZ=0 EndX=21 EndY=1.5 EndZ=0
  constraints (15):
    c: PointOnObject(g0,g-1)
    c: Radius(g0) = 1.5
    c: DistanceX(g-1,g0) = 21
    c: PointOnObject(g1,g0)
    c: PointOnObject(g1,g0)
    c: Coincident(g1,g2)
    c: PointOnObject(g2,g0)
    c: PointOnObject(g1,g-1)
    c: Coincident(g2,g3)
    c: PointOnObject(g3,g0)
    c: Coincident(g3,g4)
    c: Coincident(g4,g1)
    c: Vertical(g1,g0)
    c: Vertical(g0,g2)
    c: PointOnObject(g3,g-1)
FEATURE [PartDesign::Pocket] Pocket022  label="HorizontalScallopPocket"
  BaseFeature = -> Pocket014
  Length = 5
  Length2 = 100
  Midplane = true
  Placement = pos=(0,0,0) rot=(1,0,0;1.5708rad)
  Profile = -> Sketch040
  Type = 1
FEATURE [PartDesign::LinearPattern] LinearPattern  label="HorizontalScallopLinearPattern"
  BaseFeature = -> Pocket022
  Direction = -> Z_Axis002
  Length = 120.218
  Occurrences = 36
  Originals = -> [Pocket022]
  Placement = pos=(0,0,0) rot=(1,0,0;1.5708rad)
  expr: Occurrences = floor(Length / (<<ProjectSettings>>.ScallopRadius * 2 + <<ProjectSettings>>.DistanceBetweenScallops))
  expr: Length = <<P90Measurements>>.ButtOverallHeight
FEATURE [Sketcher::SketchObject] Sketch041  label="VerticalScallopSketch"
  FullyConstrained = true
  MapMode = 5
  Support = -> [XY_Plane002]
  expr: Constraints[0] = <<ProjectSettings>>.ScallopRadius
  expr: Constraints[1] = <<TelescoptingPadBodyPad>>.Length
  expr: Constraints[2] = <<P90Measurements>>.PadWidestWidth / 2 - <<ComfortFillet>>.Radius
  sketch-geometry (5):
    g0: Circle CenterX=-20.6159 CenterY=21 CenterZ=0 NormalX=0 NormalY=0 NormalZ=1 AngleXU=0 Radius=1.5
    g1: LineSegment StartX=-22.1159 StartY=21 StartZ=0 EndX=-20.6159 EndY=22.5 EndZ=0
    g2: LineSegment StartX=-20.6159 StartY=22.5 StartZ=0 EndX=-19.1159 EndY=21 EndZ=0
    g3: LineSegment StartX=-19.1159 StartY=21 StartZ=0 EndX=-20.6159 EndY=19.5 EndZ=0
    g4: LineSegment StartX=-20.6159 StartY=19.5 StartZ=0 EndX=-22.1159 EndY=21 EndZ=0
  constraints (15):
    c: Radius(g0) = 1.5
    c: DistanceY(g-1,g0) = 21
    c: DistanceX(g0,g-1) = 20.6159
    c: PointOnObject(g1,g0)
    c: PointOnObject(g1,g0)
    c: Coincident(g1,g2)
    c: PointOnObject(g2,g0)
    c: Coincident(g2,g3)
    c: PointOnObject(g3,g0)
    c: Coincident(g3,g4)
    c: Coincident(g4,g1)
    c: Vertical(g1,g0)
    c: Vertical(g3,g0)
    c: Horizontal(g1,g0)
    c: Horizontal(g2,g0)
FEATURE [PartDesign::Pocket] Pocket023  label="VerticalScallopPocket"
  BaseFeature = -> LinearPattern
  Length = 5
  Length2 = 100
  Midplane = true
  Placement = pos=(0,0,0) rot=(1,0,0;1.5708rad)
  Profile = -> Sketch041
  Type = 1
FEATURE [PartDesign::LinearPattern] LinearPattern002  label="VerticalScallopLinearPattern"
  BaseFeature = -> Pocket023
  Direction = -> X_Axis002
  Length = 41.2318
  Occurrences = 12
  Originals = -> [Pocket023]
  Placement = pos=(0,0,0) rot=(1,0,0;1.5708rad)
  Refine = true
  expr: Occurrences = floor(Length / (<<ProjectSettings>>.ScallopRadius * 2 + <<ProjectSettings>>.DistanceBetweenScallops))
  expr: Length = <<P90Measurements>>.PadWidestWidth - <<ComfortFillet>>.Radius * 2
FEATURE [PartDesign::Fillet] Fillet023  label="BarArmFillet"
  Base = -> LinearPattern002 [Edge253,Edge659,Edge311,Edge685]
  BaseFeature = -> LinearPattern002
  Placement = pos=(0,0,0) rot=(1,0,0;1.5708rad)
  Radius = 2
  SupportTransform = false
  expr: Radius = <<ProjectSettings>>.StandardFillet
FEATURE [Sketcher::SketchObject] Sketch042  label="PaperworkLidNubSketch"
  AttachmentOffset = pos=(0,0,60.1091) rot=(0,0,1;0rad)
  FullyConstrained = true
  MapMode = 5
  Placement = pos=(0,0,60.1091) rot=(0,0,1;0rad)
  Support = -> [XY_Plane002]
  expr: Constraints[8] = (<<P90Measurements>>.PadWidestWidth - <<ProjectSettings>>.TelescopingPadComfortFilletRadius * 3) / 2
  expr: .AttachmentOffset.Base.z = <<P90Measurements>>.ButtOverallHeight / 2
  expr: Constraints[7] = <<LightningCutPocket>>.Length
  expr: Constraints[6] = <<ProjectSettings>>.PaperworkLidNubHeight + <<ProjectSettings>>.TightTolerance * 2
  expr: Constraints[5] = <<ProjectSettings>>.PaperworkLidNubWidth + <<ProjectSettings>>.TightTolerance * 2
  sketch-geometry (3):
    g0: LineSegment StartX=-18.1159 StartY=9.8 StartZ=0 EndX=-19.8159 EndY=10.9 EndZ=0
    g1: LineSegment StartX=-19.8159 StartY=10.9 StartZ=0 EndX=-18.1159 EndY=12 EndZ=0
    g2: LineSegment StartX=-18.1159 StartY=12 StartZ=0 EndX=-18.1159 EndY=9.8 EndZ=0
  constraints (9):
    c: Coincident(g0,g1)
    c: Coincident(g1,g2)
    c: Vertical(g2)
    c: Coincident(g2,g0)
    c: Equal(g1,g0)
    c: DistanceY(g2,g2) = 2.2
    c: DistanceX(g0,g0) = 1.7
    c: DistanceY(g-1,g1) = 12
    c: DistanceX(g1,g-1) = 18.1159
FEATURE [PartDesign::SubtractivePipe] SubtractivePipe  label="PaperworkLidNubSubtractivePipe"
  AuxilleryCurvelinear = true
  AuxillerySpineTangent = false
  BaseFeature = -> Fillet023
  Binormal = (0,0,0)
  Mode = 0
  Placement = pos=(0,0,0) rot=(1,0,0;1.5708rad)
  Profile = -> Sketch042
  Spine = -> Fillet023 [Edge501]
  SpineTangent = false
  Transformation = 0
  Transition = 0
FEATURE [PartDesign::Mirrored] Mirrored002  label="PaperworkLidNubSketchMirror"
  BaseFeature = -> SubtractivePipe
  MirrorPlane = -> Sketch042 [V_Axis]
  Originals = -> [SubtractivePipe]
  Placement = pos=(0,0,0) rot=(1,0,0;1.5708rad)
FEATURE [Sketcher::SketchObject] Sketch043  label="PaperworkLidMainSketch"
  FullyConstrained = true
  MapMode = 5
  Placement = pos=(0,0,0) rot=(1,0,0;1.5708rad)
  Support = -> [XZ_Plane011]
  expr: Constraints[11] = <<ProjectSettings>>.WallThickness * 2 + <<ProjectSettings>>.LooseTolerance
  expr: Constraints[5] = <<P90Measurements>>.ButtOverallHeight - <<ProjectSettings>>.WallThickness * 2 - <<ProjectSettings>>.LooseTolerance
  expr: Constraints[2] = <<P90Measurements>>.PadWidestWidth - <<ProjectSettings>>.TelescopingPadComfortFilletRadius * 3 - <<ProjectSettings>>.LooseTolerance * 2
  sketch-geometry (6):
    g0: ArcOfCircle CenterX=1e-15 CenterY=26.1159 CenterZ=0 NormalX=0 NormalY=0 NormalZ=1 AngleXU=0 Radius=17.8159 StartAngle=3.14159 EndAngle=4.71239
    g1: LineSegment StartX=17.8159 StartY=26.1159 StartZ=0 EndX=17.8159 EndY=94.1023 EndZ=0
    g2: LineSegment StartX=-17.8159 StartY=26.1159 StartZ=0 EndX=-17.8159 EndY=94.1023 EndZ=0
    g3: ArcOfCircle CenterX=-4.4e-15 CenterY=94.1023 CenterZ=0 NormalX=0 NormalY=0 NormalZ=1 AngleXU=0 Radius=17.8159 StartAngle=1.5708 EndAngle=3.14159
    g4: ArcOfCircle CenterX=-4.4e-15 CenterY=94.1023 CenterZ=0 NormalX=0 NormalY=0 NormalZ=1 AngleXU=0 Radius=17.8159 StartAngle=0 EndAngle=1.5708
    g5: ArcOfCircle CenterX=1e-15 CenterY=26.1159 CenterZ=0 NormalX=0 NormalY=0 NormalZ=1 AngleXU=0 Radius=17.8159 StartAngle=4.71239 EndAngle=6.28319
  constraints (15):
    c: Vertical(g2)
    c: Vertical(g1)
    c: DistanceX(g2,g1) = 35.6318
    c: Tangent(g2,g3) = 1.5708
    c: Tangent(g1,g4) = -1.5708
    c: DistanceY(g-1,g3) = 111.918
    c: Tangent(g4,g3) = -1.5708
    c: PointOnObject(g3,g-2)
    c: Symmetric(g2,g1,g-2)
    c: Tangent(g1,g5) = -1.5708
    c: Tangent(g0,g2) = 1.5708
    c: DistanceY(g-1,g5) = 8.3
    c: Tangent(g0,g5) = -1.5708
    c: PointOnObject(g0,g-2)
    c: Horizontal(g0,g1)
FEATURE [PartDesign::Pad] Pad015  label="PaperworkLidMainPad"
  Direction = (1,1,1)
  Length = 1.5
  Length2 = 100
  Placement = pos=(0,0,0) rot=(1,0,0;1.5708rad)
  Profile = -> Sketch043
  Reversed = true
  Type = 0
  expr: Length = <<ProjectSettings>>.PaperworklidbaseThickness
FEATURE [Sketcher::SketchObject] Sketch044  label="PaperworkLidWallAndNubSketch"
  AttachmentOffset = pos=(0,0,60.1091) rot=(0,0,1;0rad)
  FullyConstrained = true
  MapMode = 5
  Placement = pos=(0,0,60.1091) rot=(0,0,1;0rad)
  Support = -> [XY_Plane011]
  expr: Constraints[20] = <<ProjectSettings>>.PaperwokLipInteriorWallAngle
  expr: Constraints[19] = <<ProjectSettings>>.PaperworkLipTabWallFilletRadius
  expr: Constraints[17] = <<ProjectSettings>>.PaperworkLidWallThickness
  expr: Constraints[14] = <<ProjectSettings>>.PaperworklidbaseThickness
  expr: Constraints[9] = <<ProjectSettings>>.PaperworkLidNubHeight
  expr: .AttachmentOffset.Base.z = <<P90Measurements>>.ButtOverallHeight / 2
  expr: Constraints[6] = (<<P90Measurements>>.PadWidestWidth - <<ProjectSettings>>.TelescopingPadComfortFilletRadius * 3 - <<ProjectSettings>>.LooseTolerance * 2) / 2
  expr: Constraints[10] = <<LightningCutPocket>>.Length - <<ProjectSettings>>.LooseTolerance
  expr: Constraints[8] = <<ProjectSettings>>.PaperworkLidNubWidth
  sketch-geometry (7):
    g0: LineSegment StartX=-17.8159 StartY=0 StartZ=0 EndX=-17.8159 EndY=9.7 EndZ=0
    g1: LineSegment StartX=-17.8159 StartY=9.7 StartZ=0 EndX=-19.3159 EndY=10.7 EndZ=0
    g2: LineSegment StartX=-19.3159 StartY=10.7 StartZ=0 EndX=-17.8159 EndY=11.7 EndZ=0
    g3: LineSegment StartX=-17.8159 StartY=11.7 StartZ=0 EndX=-15.8159 EndY=11.7 EndZ=0
    g4: ArcOfCircle CenterX=-9.30257 CenterY=5.5 CenterZ=0 NormalX=0 NormalY=0 NormalZ=1 AngleXU=0 Radius=4 StartAngle=3.49066 EndAngle=4.71239
    g5: LineSegment StartX=-13.0613 StartY=4.13192 StartZ=0 EndX=-15.8159 EndY=11.7 EndZ=0
    g6: LineSegment StartX=-17.8159 StartY=0 StartZ=0 EndX=-9.30257 EndY=1.5 EndZ=0
  constraints (21):
    c: PointOnObject(g0,g-1)
    c: Vertical(g0)
    c: Coincident(g0,g1)
    c: Coincident(g1,g2)
    c: Coincident(g2,g3)
    c: Horizontal(g3)
    c: DistanceX(g0,g-1) = 17.8159
    c: Equal(g1,g2)
    c: DistanceY(g0,g2) = 2
    c: DistanceX(g1,g0) = 1.5
    c: DistanceY(g-1,g3) = 11.7
    c: Vertical(g2,g0)
    c: Coincident(g5,g3)
    c: Tangent(g5,g4) = 1.5708
    c: DistanceY(g6,g4) = 1.5
    c: Vertical(g4,g4)
    c: Coincident(g6,g4)
    c: DistanceX(g3,g3) = 2
    c: Coincident(g6,g0)
    c: Radius(g4) = 4
    c: Angle(g3,g5) = 1.91986
FEATURE [PartDesign::AdditivePipe] AdditivePipe  label="PaperworkLidWallAndNubAdditivePipe"
  AuxilleryCurvelinear = true
  AuxillerySpineTangent = false
  BaseFeature = -> Pad015
  Binormal = (0,0,0)
  Mode = 0
  Placement = pos=(0,0,0) rot=(1,0,0;1.5708rad)
  Profile = -> Sketch044
  Spine = -> Pad015 [Edge17]
  SpineTangent = false
  Transformation = 0
  Transition = 0
FEATURE [PartDesign::Mirrored] Mirrored003  label="PaperworkLidWallAndNubMirrored"
  BaseFeature = -> AdditivePipe
  MirrorPlane = -> Sketch044 [V_Axis]
  Originals = -> [AdditivePipe]
  Placement = pos=(0,0,0) rot=(1,0,0;1.5708rad)
  Refine = true
FEATURE [Sketcher::SketchObject] Sketch045  label="PaperworkLidCrosspinSlotSketch"
  FullyConstrained = true
  MapMode = 5
  Placement = pos=(0,0,0) rot=(0.57735,0.57735,0.57735;2.0944rad)
  Support = -> [YZ_Plane011]
  expr: Constraints[8] = <<LightningCutPocket>>.Length
  expr: Constraints[2] = <<ProjectSettings>>.CrosspinWidth + <<ProjectSettings>>.LooseTolerance * 2
  expr: Constraints[1] = <<TelescopingPadSettings>>.TelescopingBarInsertDepth / 2 + <<ProjectSettings>>.TightTolerance * 2
  expr: Constraints[0] = <<P90Measurements>>.PadWidestWidthOuterShoulderDistanceFromReferencePoint + <<ProjectSettings>>.BarHeight / 2 + <<ProjectSettings>>.TightTolerance
  expr: Constraints[14] = <<ProjectSettings>>.StandardFillet
  sketch-geometry (10):
    g0: ArcOfCircle CenterX=5.8875 CenterY=78.339 CenterZ=0 NormalX=0 NormalY=0 NormalZ=1 AngleXU=0 Radius=2.3 StartAngle=1.5708 EndAngle=4.71239
    g1: LineSegment StartX=5.8875 StartY=80.639 StartZ=0 EndX=10 EndY=80.639 EndZ=0
    g2: LineSegment StartX=12 StartY=80.639 StartZ=0 EndX=12 EndY=76.039 EndZ=0
    g3: LineSegment StartX=10 StartY=76.039 StartZ=0 EndX=5.8875 EndY=76.039 EndZ=0
    g4: LineSegment StartX=12 StartY=80.639 StartZ=0 EndX=12 EndY=82.639 EndZ=0
    g5: ArcOfCircle CenterX=10 CenterY=82.639 CenterZ=0 NormalX=0 NormalY=0 NormalZ=1 AngleXU=0 Radius=2 StartAngle=4.71239 EndAngle=6.28319
    g6: GeomPoint X=12 Y=80.639 Z=0
    g7: LineSegment StartX=12 StartY=76.039 StartZ=0 EndX=12 EndY=74.039 EndZ=0
    g8: ArcOfCircle CenterX=10 CenterY=74.039 CenterZ=0 NormalX=0 NormalY=0 NormalZ=1 AngleXU=0 Radius=2 StartAngle=2.7e-15 EndAngle=1.5708
    g9: GeomPoint X=12 Y=76.039 Z=0
  constraints (25):
    c: DistanceY(g-1,g0) = 78.339
    c: DistanceX(g-1,g0) = 5.8875
    c: Diameter(g0) = 4.6
    c: Coincident(g6,g2)
    c: Coincident(g2,g9)
    c: Horizontal(g1)
    c: Horizontal(g3)
    c: Vertical(g2)
    c: DistanceX(g-1,g6) = 12
    c: Vertical(g3,g0)
    c: Coincident(g0,g1)
    c: Coincident(g0,g3)
    c: Vertical(g0,g0)
    c: Vertical(g4)
    c: DistanceY(g6,g4) = 2
    c: PointOnObject(g6,g1)
    c: Tangent(g1,g5) = -1.5708
    c: Coincident(g4,g2)
    c: Tangent(g5,g4) = -1.5708
    c: Vertical(g7)
    c: PointOnObject(g9,g3)
    c: Tangent(g3,g8) = -1.5708
    c: Coincident(g7,g2)
    c: Tangent(g8,g7) = 1.5708
    c: Equal(g8,g5)
FEATURE [PartDesign::Pocket] Pocket024  label="PaperworkLidCrosspinSlotPocket"
  BaseFeature = -> Mirrored003
  Length = 5
  Length2 = 100
  Midplane = true
  Placement = pos=(0,0,0) rot=(1,0,0;1.5708rad)
  Profile = -> Sketch045
  Type = 1
FEATURE [Sketcher::SketchObject] Sketch046  label="PaperworkLidFingerHoleSketch"
  AttachmentOffset = pos=(0,0,60.1091) rot=(0,0,1;0rad)
  FullyConstrained = false
  MapMode = 5
  Placement = pos=(0,0,60.1091) rot=(0,0,1;0rad)
  Support = -> [XY_Plane011]
  expr: .AttachmentOffset.Base.z = <<P90Measurements>>.ButtOverallHeight / 2
  expr: Constraints[7] = <<ProjectSettings>>.PaperworkLidFingerHoleDiameter / 2
  expr: Constraints[6] = <<ProjectSettings>>.PaperworklidbaseThickness
  sketch-geometry (7):
    g0: LineSegment StartX=0 StartY=0 StartZ=0 EndX=10 EndY=0 EndZ=0
    g1: LineSegment StartX=10 StartY=1.5 StartZ=0 EndX=0 EndY=1.5 EndZ=0
    g2: LineSegment StartX=0 StartY=1.5 StartZ=0 EndX=0 EndY=0 EndZ=0
    g3: ArcOfCircle CenterX=10 CenterY=0.75 CenterZ=0 NormalX=0 NormalY=0 NormalZ=1 AngleXU=0 Radius=0.75 StartAngle=1.5708 EndAngle=4.71239
    g4: LineSegment StartX=0 StartY=1.5 StartZ=0 EndX=0 EndY=8.15565 EndZ=0
    g5: LineSegment StartX=0 StartY=8.15565 StartZ=0 EndX=10 EndY=8.15565 EndZ=0
    g6: LineSegment StartX=10 StartY=8.15565 StartZ=0 EndX=10 EndY=1.5 EndZ=0
  constraints (19):
    c: Coincident(g1,g2)
    c: Coincident(g2,g0)
    c: Horizontal(g0)
    c: Horizontal(g1)
    c: Vertical(g2)
    c: Coincident(g0,g-1)
    c: DistanceY(g2,g2) = 1.5
    c: DistanceX(g1,g1) = 10
    c: Coincident(g3,g1)
    c: Coincident(g3,g0)
    c: Vertical(g3,g0)
    c: Vertical(g0,g1)
    c: Coincident(g1,g4)
    c: PointOnObject(g4,g-2)
    c: Coincident(g4,g5)
    c: Horizontal(g5)
    c: Coincident(g5,g6)
    c: Vertical(g6)
    c: Coincident(g6,g1)
FEATURE [PartDesign::Groove] Groove  label="PaperworkLidFingerHoleGroove"
  Angle = 360
  Axis = (0,1,0)
  Base = (0,0,60.1091)
  BaseFeature = -> Pocket024
  Placement = pos=(0,0,0) rot=(1,0,0;1.5708rad)
  Profile = -> Sketch046
  ReferenceAxis = -> Sketch046 [V_Axis]
FEATURE [PartDesign::Body] Body008  label="PaperworkLid"
  Group = -> [Sketch043,Pad015,Sketch044,AdditivePipe,Mirrored003,Sketch045,Pocket024,Sketch046,Groove]
  Origin = -> Origin011
  Placement = pos=(0,18,0) rot=(0,0,1;0rad)
  Tip = -> Groove
  expr: .Placement.Base.y = <<PadBodyPad>>.Length
FEATURE [PartDesign::Fillet] Fillet024  label="interior fillet"
  Base = -> Mirrored002 [Edge201,Edge25,Edge186]
  BaseFeature = -> Mirrored002
  Placement = pos=(0,0,0) rot=(1,0,0;1.5708rad)
  Radius = 1
  SupportTransform = false
FEATURE [PartDesign::Body] Body002  label="TelescopingPad"
  Group = -> [Sketch008,Pad006,Sketch009,Pocket002,Sketch010,Pad007,Sketch011,Mirrored,Pocket003,Fillet,Sketch029,Pocket014,Sketch040,Pocket022,LinearPattern,Sketch041,Pocket023,LinearPattern002,Fillet023,Sketch042,SubtractivePipe,Mirrored002,Fillet024]
  Origin = -> Origin002
  Placement = pos=(0,18,0) rot=(0,0,1;0rad)
  Tip = -> Fillet024
  expr: .Placement.Base.y = <<PadBodyPad>>.Length
FEATURE [Sketcher::SketchObject] Sketch047  label="BarEndcapSketch"
  FullyConstrained = true
  MapMode = 5
  Placement = pos=(0,-265,-5.88e-14) rot=(1,0,0;1.5708rad)
  Support = -> [Pocket012]
  expr: Constraints[6] = <<ProjectSettings>>.BarThickness / 2
  expr: Constraints[2] = <<ProjectSettings>>.BarHeight
  expr: Constraints[5] = <<CentralPadTelescopingBarInsertArmSketch>>.Constraints.BarArmWallThickness
  sketch-geometry (4):
    g0: ArcOfCircle CenterX=2.5 CenterY=2.93 CenterZ=0 NormalX=0 NormalY=0 NormalZ=1 AngleXU=0 Radius=4.57 StartAngle=0 EndAngle=1.5708
    g1: ArcOfCircle CenterX=2.5 CenterY=-2.93 CenterZ=0 NormalX=0 NormalY=0 NormalZ=1 AngleXU=0 Radius=4.57 StartAngle=4.71239 EndAngle=6.28319
    g2: LineSegment StartX=2.5 StartY=7.5 StartZ=0 EndX=2.5 EndY=-7.5 EndZ=0
    g3: LineSegment StartX=7.07 StartY=2.93 StartZ=0 EndX=7.07 EndY=-2.93 EndZ=0
  constraints (9):
    c: Tangent(g1,g3) = 1.5708
    c: Tangent(g3,g0) = 1.5708
    c: DistanceY(g2,g2) = 15
    c: Symmetric(g2,g2,g-1)
    c: Symmetric(g1,g0,g-1)
    c: DistanceX(g2,g0) = 4.57
    c: DistanceX(g-1,g2) = 2.5
    c: Perpendicular(g0,g2) = 1.5708
    c: Coincident(g1,g2)
FEATURE [PartDesign::Pad] Pad016  label="BarEndcapPad"
  BaseFeature = -> Pocket012
  Direction = (1,1,1)
  Length = 4.9
  Length2 = 100
  Placement = pos=(0,0,0) rot=(1,0,0;1.5708rad)
  Profile = -> Sketch047
  Reversed = true
  Type = 0
  expr: Length = <<ProjectSettings>>.BarThickness - <<ProjectSettings>>.TightTolerance
FEATURE [Sketcher::SketchObject] Sketch048  label="BarReinforcmentSketch"
  FullyConstrained = true
  MapMode = 5
  Placement = pos=(0,-260.1,0) rot=(-1,0,0;1.5708rad)
  Support = -> [Pad016]
  expr: Constraints[9] = <<ProjectSettings>>.BarThickness / 2
  expr: Constraints[8] = <<ProjectSettings>>.BarHeight / 3
  expr: Constraints[7] = <<CentralPadTelescopingBarInsertArmSketch>>.Constraints.BarArmWallThickness
  sketch-geometry (4):
    g0: LineSegment StartX=2.5 StartY=2.5 StartZ=0 EndX=7.07 EndY=2.5 EndZ=0
    g1: LineSegment StartX=7.07 StartY=2.5 StartZ=0 EndX=7.07 EndY=-2.5 EndZ=0
    g2: LineSegment StartX=7.07 StartY=-2.5 StartZ=0 EndX=2.5 EndY=-2.5 EndZ=0
    g3: LineSegment StartX=2.5 StartY=-2.5 StartZ=0 EndX=2.5 EndY=2.5 EndZ=0
  constraints (11):
    c: Coincident(g0,g1)
    c: Coincident(g1,g2)
    c: Coincident(g2,g3)
    c: Coincident(g3,g0)
    c: Horizontal(g0)
    c: Horizontal(g2)
    c: Vertical(g3)
    c: DistanceX(g0,g0) = 4.57
    c: DistanceY(g1,g1) = 5
    c: DistanceX(g-1,g2) = 2.5
    c: Symmetric(g0,g1,g-1)
FEATURE [PartDesign::Pad] Pad017  label="BarReinforcmentPad"
  BaseFeature = -> Pad016
  Direction = (1,1,1)
  Length = 247.9
  Length2 = 100
  Placement = pos=(0,0,0) rot=(1,0,0;1.5708rad)
  Profile = -> Sketch048
  Refine = true
  Type = 0
  expr: Length = <<ProjectSettings>>.BarLength - <<ProjectSettings>>.BarRackStartOffset + <<ProjectSettings>>.WallThickness - <<ProjectSettings>>.TightTolerance
FEATURE [PartDesign::Fillet] Fillet025  label="2mm fillet"
  Base = -> Pad017 [Edge100,Edge89,Edge77,Edge111,Edge122,Edge133,Edge144,Edge58,Edge2,Edge161,Edge178,Edge177]
  BaseFeature = -> Pad017
  Placement = pos=(0,0,0) rot=(1,0,0;1.5708rad)
  Radius = 2
  SupportTransform = false
FEATURE [Sketcher::SketchObject] Sketch049  label="LockingButtonOverhangCompensationSketch"
  AttachmentOffset = pos=(0,0,-4) rot=(0,0,1;0rad)
  FullyConstrained = true
  MapMode = 5
  Placement = pos=(0,4,9e-16) rot=(1,0,0;1.5708rad)
  Support = -> [XZ_Plane]
  expr: Constraints[8] = <<LockingButtonHolePocket>>.Length
  expr: .AttachmentOffset.Base.z = -1 * <<ProjectSettings>>.WallThickness
  expr: Constraints[7] = <<ProjectSettings>>.LockingButtonWidth + <<ProjectSettings>>.LooseTolerance * 2
  sketch-geometry (3):
    g0: LineSegment StartX=-5.3 StartY=111.914 StartZ=0 EndX=5.3 EndY=111.914 EndZ=0
    g1: LineSegment StartX=5.3 StartY=111.914 StartZ=0 EndX=0 EndY=117.214 EndZ=0
    g2: LineSegment StartX=0 StartY=117.214 StartZ=0 EndX=-5.3 EndY=111.914 EndZ=0
  constraints (9):
    c: Horizontal(g0)
    c: Coincident(g0,g1)
    c: PointOnObject(g1,g-2)
    c: Coincident(g1,g2)
    c: Coincident(g2,g0)
    c: Angle(g0,g2) = 0.785398
    c: Equal(g2,g1)
    c: DistanceX(g0,g0) = 10.6
    c: DistanceY(g-1,g0) = 111.914
FEATURE [PartDesign::Pocket] Pocket025  label="LockingButtonOverhangCompensationPocket"
  BaseFeature = -> Fillet017
  Length = 10.6
  Length2 = 100
  Placement = pos=(0,0,0) rot=(1,0,0;1.5708rad)
  Profile = -> Sketch049
  Type = 0
  expr: Length = <<ProjectSettings>>.LockingButtonHeight + <<ProjectSettings>>.LooseTolerance * 2
FEATURE [Sketcher::SketchObject] Sketch050  label="LockingPinHoleOverhangSketch"
  FullyConstrained = true
  MapMode = 5
  Placement = pos=(0,0,0) rot=(0.57735,0.57735,0.57735;2.0944rad)
  Support = -> [YZ_Plane]
  expr: Constraints[11] = <<P90Measurements>>.PadWidestWidthOuterShoulderDistanceFromReferencePoint + <<TelescopingBarSettings>>.BarHeight + <<TelescopingBarSettings>>.LockingPinHeight + <<ProjectSettings>>.LooseTolerance * 2
  expr: Constraints[10] = <<ProjectSettings>>.WallThickness
  expr: Constraints[9] = <<P90Measurements>>.PadWidestWidthOuterShoulderDistanceFromReferencePoint + (<<TelescopingBarSettings>>.BarHeight - <<TelescopingBarSettings>>.LockingPinHeight) / 2
  expr: Constraints[8] = <<ProjectSettings>>.LockingPinWidth + <<ProjectSettings>>.LooseTolerance * 2
  sketch-geometry (6):
    g0: LineSegment StartX=4 StartY=90.039 StartZ=0 EndX=9.3625 EndY=90.039 EndZ=0
    g1: LineSegment StartX=9.3625 StartY=90.039 StartZ=0 EndX=9.3625 EndY=74.089 EndZ=0
    g2: LineSegment StartX=9.3625 StartY=74.089 StartZ=0 EndX=4 EndY=74.089 EndZ=0
    g3: LineSegment StartX=4 StartY=74.089 StartZ=0 EndX=4 EndY=90.039 EndZ=0
    g4: LineSegment StartX=4 StartY=90.039 StartZ=0 EndX=6.68125 EndY=92.7202 EndZ=0
    g5: LineSegment StartX=6.68125 StartY=92.7202 StartZ=0 EndX=9.3625 EndY=90.039 EndZ=0
  constraints (17):
    c: Coincident(g0,g1)
    c: Coincident(g1,g2)
    c: Coincident(g2,g3)
    c: Coincident(g3,g0)
    c: Horizontal(g0)
    c: Horizontal(g2)
    c: Vertical(g1)
    c: Vertical(g3)
    c: DistanceX(g0,g0) = 5.3625
    c: DistanceY(g-1,g2) = 74.089
    c: DistanceX(g-1,g2) = 4
    c: DistanceY(g-1,g0) = 90.039
    c: Coincident(g0,g4)
    c: Coincident(g4,g5)
    c: Coincident(g5,g0)
    c: Equal(g4,g5)
    c: Angle(g0,g4) = 0.785398
FEATURE [PartDesign::Pocket] Pocket026  label="LockingPinHoleOverhangPocket"
  BaseFeature = -> Pocket025
  Length = 62.0468
  Length2 = 100
  Midplane = true
  Placement = pos=(0,0,0) rot=(1,0,0;1.5708rad)
  Profile = -> Sketch050
  Type = 0
  expr: Length = <<LockingPinHolePocket>>.Length
FEATURE [PartDesign::Body] Body  label="LockingBody"
  Group = -> [Sketch,Pad,Sketch001,Pad001,Sketch002,Pocket,Sketch003,Pad002,Sketch004,Pocket001,Sketch014,Pad008,Mirrored001,Sketch018,Pocket007,Sketch019,Pocket008,Sketch022,Pocket010,Fillet016,Fillet017,Sketch049,Pocket025,Sketch050,Pocket026]
  Origin = -> Origin
  Tip = -> Pocket026
FEATURE [Sketcher::SketchObject] Sketch052  label="CrosspinMainBodySketch"
  FullyConstrained = true
  MapMode = 5
  Placement = pos=(0,0,0) rot=(0.57735,0.57735,0.57735;2.0944rad)
  Support = -> [YZ_Plane012]
  expr: Constraints[19] = <<ProjectSettings>>.CrosspinWidth - <<ProjectSettings>>.TightTolerance * 2
  sketch-geometry (7):
    g0: LineSegment StartX=-1.9 StartY=0 StartZ=0 EndX=-0.95 EndY=-1.64545 EndZ=0
    g1: LineSegment StartX=-0.95 StartY=-1.64545 StartZ=0 EndX=0.95 EndY=-1.64545 EndZ=0
    g2: LineSegment StartX=0.95 StartY=-1.64545 StartZ=0 EndX=1.9 EndY=-2e-16 EndZ=0
    g3: LineSegment StartX=1.9 StartY=-2e-16 StartZ=0 EndX=0.95 EndY=1.64545 EndZ=0
    g4: LineSegment StartX=0.95 StartY=1.64545 StartZ=0 EndX=-0.95 EndY=1.64545 EndZ=0
    g5: LineSegment StartX=-0.95 StartY=1.64545 StartZ=0 EndX=-1.9 EndY=0 EndZ=0
    g6: Circle CenterX=0 CenterY=0 CenterZ=0 NormalX=0 NormalY=0 NormalZ=1 AngleXU=0 Radius=1.9
  constraints (16):
    c: Coincident(g0,g1)
    c: Coincident(g1,g2)
    c: Coincident(g2,g3)
    c: Coincident(g3,g4)
    c: Coincident(g4,g5)
    c: Coincident(g5,g0)
    c: Equal(g0, g1-g5) x5
    c: PointOnObject(g0,g6)
    c: PointOnObject(g1,g6)
    c: PointOnObject(g2,g6)
    c: PointOnObject(g3,g6)
    c: PointOnObject(g4,g6)
    c: PointOnObject(g5,g6)
    c: Coincident(g6,g-1)
    c: PointOnObject(g5,g-1)
    c: DistanceX(g0,g2) = 3.8
FEATURE [PartDesign::Pad] Pad018  label="CrosspinMainBodyPad"
  Direction = (1,1,1)
  Length = 17
  Length2 = 100
  Placement = pos=(0,0,0) rot=(0.57735,0.57735,0.57735;2.0944rad)
  Profile = -> Sketch052
  Type = 0
  expr: Length = <<ProjectSettings>>.PadCrosspinLength
FEATURE [PartDesign::Chamfer] Chamfer  label="InserttionChamfer"
  Angle = 45
  Base = -> Pad018 [Face7]
  BaseFeature = -> Pad018
  ChamferType = 0
  FlipDirection = false
  Placement = pos=(0,0,0) rot=(0.57735,0.57735,0.57735;2.0944rad)
  Size = 1
  Size2 = 1
  SupportTransform = false
FEATURE [PartDesign::Body] Body009  label="PadCrosspin"
  Group = -> [Sketch052,Pad018,Chamfer]
  Origin = -> Origin012
  Placement = pos=(18,23.8875,78.339) rot=(0,0,1;0rad)
  Tip = -> Chamfer
  expr: .Placement.Base.y = <<TelescopingPadSettings>>.TelescopingBarInsertDepth / 2 + <<ProjectSettings>>.TightTolerance * 2 + <<ProjectSettings>>.LockingBodyPadThickness
  expr: .Placement.Base.z = <<P90Measurements>>.PadWidestWidthOuterShoulderDistanceFromReferencePoint + <<ProjectSettings>>.BarHeight / 2 + <<ProjectSettings>>.TightTolerance
FEATURE [PartDesign::Fillet] Fillet026  label="1point5mmfillet"
  Base = -> Fillet025 [Edge224,Edge68,Edge210,Edge63,Edge13,Edge25,Edge37,Edge49,Edge46,Edge34,Edge22,Edge10,Edge8]
  BaseFeature = -> Fillet025
  Placement = pos=(0,0,0) rot=(1,0,0;1.5708rad)
  Radius = 1.5
  SupportTransform = false
FEATURE [PartDesign::Body] Body006  label="RightTelescopingBar"
  Group = -> [Sketch025,Pad013,Sketch024,Pocket011,Sketch027,Pocket013,LinearPattern001,Sketch028,Pocket012,Sketch047,Pad016,Sketch048,Pad017,Fillet025,Fillet026]
  Origin = -> Origin007
  Placement = pos=(-28.4159,30,78.289) rot=(0,1,0;3.14159rad)
  Tip = -> Fillet026
  expr: .Placement.Base.z = <<P90Measurements>>.PadWidestWidthOuterShoulderDistanceFromReferencePoint + <<ProjectSettings>>.BarHeight / 2 + <<ProjectSettings>>.TightTolerance / 2
  expr: .Placement.Base.x = -1 * (<<P90Measurements>>.PadWidestWidth / 2 + <<ProjectSettings>>.BarThickness / 2) - <<ProjectSettings>>.LooseTolerance
  expr: .Placement.Base.y = <<ProjectSettings>>.WallThickness * 4 + <<ProjectSettings>>.LockingButtonWidth + <<ProjectSettings>>.CrosspinWidth
FEATURE [Part::Mirroring] Part__Mirroring  label="LeftTelescopingBar"
  Base = (7.62939e-06,-102.5,78.339)
  Normal = (1,0,-1.19209e-07)
  Source = -> Body006
FEATURE [App::Part] Part  label="TelescopingArray"
  Group = -> [Body002,Body008,Body006,Part__Mirroring,Body009]
  Origin = -> Origin003
  Placement = pos=(0,205,0) rot=(0,0,1;0rad)
FEATURE [PartDesign::Fillet] Fillet027
  Base = -> Fillet004 [Edge3]
  BaseFeature = -> Fillet004
  Placement = pos=(0,0,0) rot=(0.57735,0.57735,0.57735;2.0944rad)
  Radius = 1
  SupportTransform = false
FEATURE [PartDesign::Body] Body004  label="LockingPin"
  Group = -> [Sketch017,Pad010,Fillet004,Fillet027]
  Origin = -> Origin005
  Placement = pos=(0,6.48125,80.139) rot=(0,0,1;0rad)
  Tip = -> Fillet027
  expr: .Placement.Base.y = <<ProjectSettings>>.WallThickness + <<ProjectSettings>>.LockingPinWidth / 2 + <<ProjectSettings>>.TightTolerance
  expr: .Placement.Base.z = <<P90Measurements>>.PadWidestWidthOuterShoulderDistanceFromReferencePoint + <<TelescopingBarSettings>>.BarHeight - <<TelescopingBarSettings>>.LockingPinHeight / 2 - <<ProjectSettings>>.LooseTolerance
FEATURE [App::Part] Part002  label="LockingMechanism"
  Group = -> [Body005,Body004]
  Origin = -> Origin009
  Placement = pos=(0,0,6.5) rot=(0,0,1;0rad)
FEATURE [Sketcher::SketchObject] Sketch053  label="LockingBodySupportBaseSketch"
  FullyConstrained = true
  MapMode = 5
  Placement = pos=(0,0,0) rot=(1,0,0;1.5708rad)
  Support = -> [XZ_Plane013]
  expr: Constraints[20] = <<P90Measurements>>.ButtOverallHeight
  expr: Constraints[24] = <<P90Measurements>>.PadWidestWidthInnerShoulderDistanceFromReferencePoint - 5mm
  expr: Constraints[25] = <<P90Measurements>>.PadBottomWidth
  expr: Constraints[23] = <<P90Measurements>>.PadThinnestWidth
  expr: Constraints[22] = <<P90Measurements>>.PadWidestWidth
  sketch-geometry (17):
    g0: ArcOfCircle CenterX=-3.81 CenterY=18.6944 CenterZ=0 NormalX=0 NormalY=0 NormalZ=1 AngleXU=0 Radius=18.6944 StartAngle=3.14159 EndAngle=4.71239
    g1: ArcOfCircle CenterX=3.81 CenterY=18.6944 CenterZ=0 NormalX=0 NormalY=0 NormalZ=1 AngleXU=0 Radius=18.6944 StartAngle=4.71239 EndAngle=6.28319
    g2: ArcOfCircle CenterX=-5e-16 CenterY=94.6023 CenterZ=0 NormalX=0 NormalY=0 NormalZ=1 AngleXU=0 Radius=25.6159 StartAngle=1.5708 EndAngle=3.14159
    g3: ArcOfCircle CenterX=-5e-16 CenterY=94.6023 CenterZ=0 NormalX=0 NormalY=0 NormalZ=1 AngleXU=0 Radius=25.6159 StartAngle=0 EndAngle=1.5708
    g4: LineSegment StartX=-25.6159 StartY=94.6023 StartZ=0 EndX=-25.6159 EndY=59.3128 EndZ=0
    g5: LineSegment StartX=-25.6159 StartY=59.3128 StartZ=0 EndX=-22.5044 EndY=59.3128 EndZ=0
    g6: LineSegment StartX=-22.5044 StartY=59.3128 StartZ=0 EndX=-22.5044 EndY=18.6944 EndZ=0
    g7: LineSegment StartX=-3.81 StartY=0 StartZ=0 EndX=3.81 EndY=0 EndZ=0
    g8: LineSegment StartX=22.5044 StartY=18.6944 StartZ=0 EndX=22.5044 EndY=59.3128 EndZ=0
    g9: LineSegment StartX=22.5044 StartY=59.3128 StartZ=0 EndX=25.6159 EndY=59.3128 EndZ=0
    g10: LineSegment StartX=25.6159 StartY=59.3128 StartZ=0 EndX=25.6159 EndY=94.6023 EndZ=0
    g11: LineSegment StartX=-22.5044 StartY=18.6944 StartZ=0 EndX=-25.6159 EndY=18.6944 EndZ=0
    g12: LineSegment StartX=22.5044 StartY=18.6944 StartZ=0 EndX=25.6159 EndY=18.6944 EndZ=0
    g13: LineSegment StartX=-25.6159 StartY=0 StartZ=0 EndX=-25.6159 EndY=18.6944 EndZ=0
    g14: LineSegment StartX=25.6159 StartY=18.6944 StartZ=0 EndX=25.6159 EndY=0 EndZ=0
    g15: LineSegment StartX=-3.81 StartY=0 StartZ=0 EndX=-25.6159 EndY=0 EndZ=0
    g16: LineSegment StartX=3.81 StartY=0 StartZ=0 EndX=25.6159 EndY=0 EndZ=0
  constraints (43):
    c: Symmetric(g13,g14,g-2)
    c: PointOnObject(g0,g-1)
    c: PointOnObject(g1,g-1)
    c: Vertical(g4)
    c: Coincident(g5,g4)
    c: Vertical(g6)
    c: Vertical(g8)
    c: Coincident(g9,g8)
    c: Vertical(g10)
    c: Coincident(g9,g10)
    c: Horizontal(g9)
    c: Tangent(g2,g4) = -1.5708
    c: Tangent(g3,g10) = -1.5708
    c: Tangent(g6,g0) = -1.5708
    c: Tangent(g7,g0) = -1.5708
    c: Tangent(g7,g1) = -1.5708
    c: Tangent(g8,g1) = -1.5708
    c: Symmetric(g8,g6,g-2)
    c: Symmetric(g4,g9,g-2)
    c: Coincident(g6,g5)
    c: DistanceY(g-1,g3) = 120.218
    c: Equal(g1,g0)
    c: DistanceX(g2,g3) = 51.2318
    c: DistanceX(g5,g8) = 45.0088
    c: DistanceY(g-1,g8) = 59.3128
    c: DistanceX(g7,g7) = 7.62
    c: PointOnObject(g2,g-2)
    c: Tangent(g2,g3) = -1.5708
    c: Equal(g4,g10)
    c: Coincident(g11,g0)
    c: Horizontal(g11)
    c: Coincident(g12,g1)
    c: Horizontal(g12)
    c: Vertical(g13)
    c: Coincident(g13,g11)
    c: Coincident(g14,g12)
    c: Vertical(g14)
    c: Vertical(g12,g9)
    c: Coincident(g15,g0)
    c: Coincident(g15,g13)
    c: Horizontal(g15)
    c: Coincident(g16,g1)
    c: Coincident(g16,g14)
FEATURE [PartDesign::Pad] Pad019
  Direction = (1,1,1)
  Length = 18
  Length2 = 100
  Placement = pos=(0,0,0) rot=(1,0,0;1.5708rad)
  Profile = -> Sketch053
  Reversed = true
  Type = 0
  expr: Length = <<PadBodyPad>>.Length
FEATURE [PartDesign::Body] Body010  label="LockingBodySupport"
  Group = -> [Sketch053,Pad019]
  Origin = -> Origin013
  Placement = pos=(-0.16,0,0) rot=(0,0,1;0rad)
  Tip = -> Pad019
  expr: .Placement.Base.x = -1 * <<ProjectSettings>>.SupportGap
FEATURE [Part::Mirroring] Part__Mirroring001  label="LockingBodySupport Mirror"
  Base = (0,0,0)
  Normal = (1,0,0)
  Source = -> Body010
FEATURE [App::Part] Part001  label="LockingAssembly"
  Group = -> [Body,Part002,Body010,Part__Mirroring001]
  Origin = -> Origin008
  Placement = pos=(0,205,0) rot=(0,0,1;0rad)
